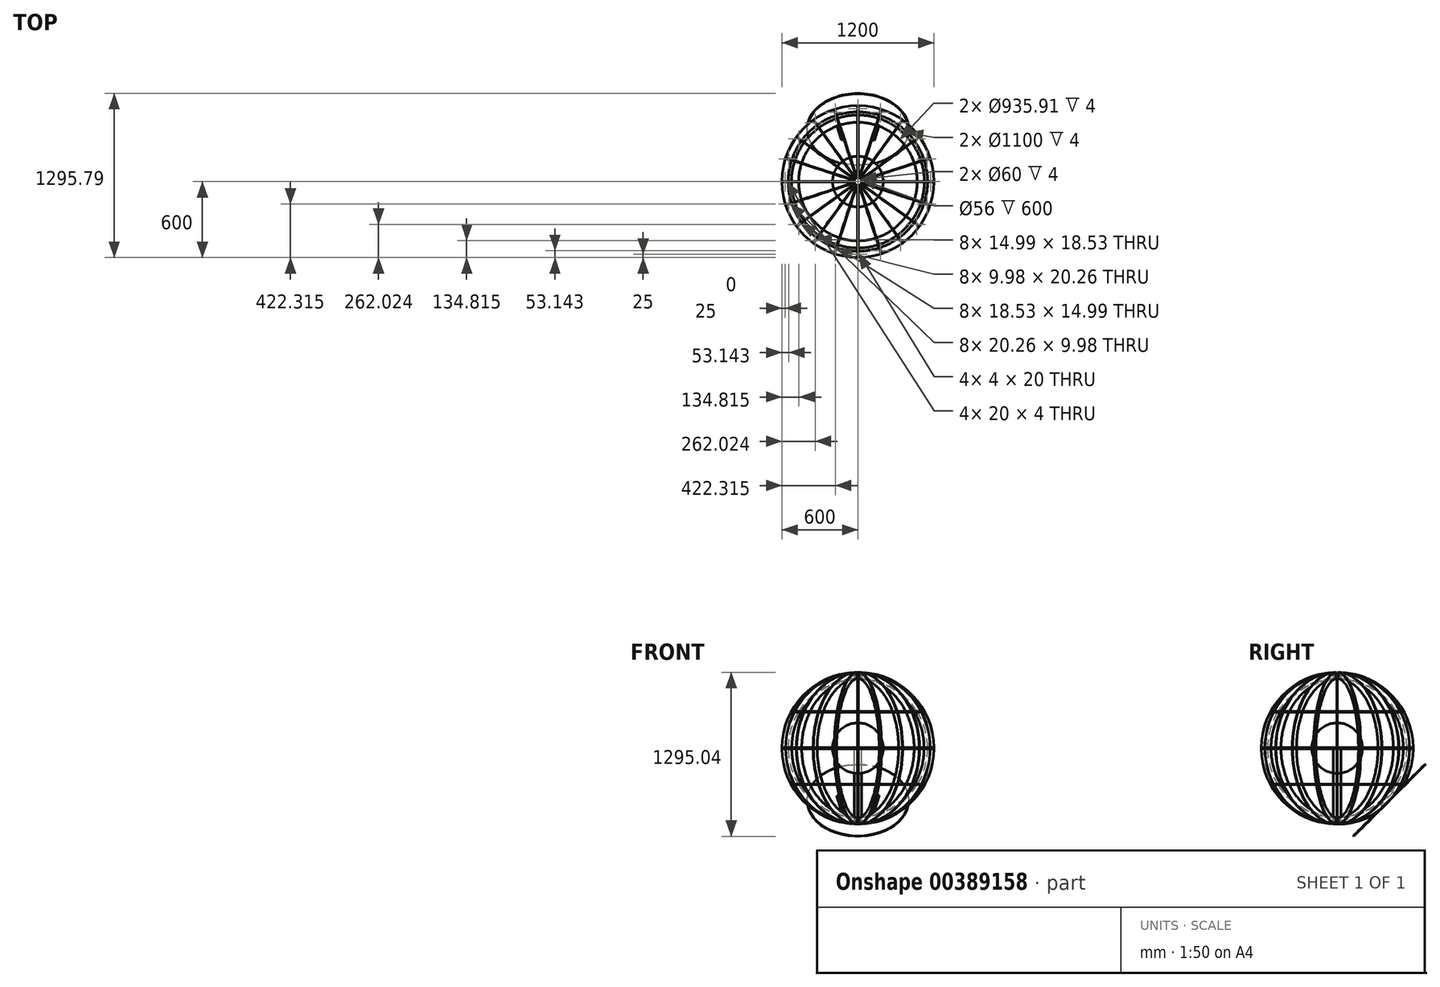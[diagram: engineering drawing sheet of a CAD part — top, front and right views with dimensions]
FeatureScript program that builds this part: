
annotation { "Feature Type Name" : "Feature", "Feature Type Description" : "" }
export const myFeature = defineFeature(function(context is Context, id is Id, definition is map)
    precondition{}
    {
        {
            var Q0;
            Q0=qCreatedBy(makeId("Front.planeOp"),FACE);
            var sketch = newSketch(context, id + "F0", { "sketchPlane" : qUnion([Q0])});
            skArc(sketch, "E0", {"start": v(-600, 0) * mm, "mid": v(-424.26, -424.26) * mm, "end": v(0, -600) * mm});
            skArc(sketch, "E1", {"start": v(-550, 0) * mm, "mid": v(-529.88, -147.4) * mm, "end": v(-471, -284) * mm});
            skLineSegment(sketch, "E2", {"start": v(0, 0) * mm, "end": v(0, -799.31) * mm});
            skLineSegment(sketch, "E3", {"start": v(0, 0) * mm, "end": v(-600, 0) * mm});
            skLineSegment(sketch, "E4", {"start": v(-599.99, -4) * mm, "end": v(-585, -4) * mm});
            skLineSegment(sketch, "E5", {"start": v(-585, -4) * mm, "end": v(-585, -2) * mm});
            skLineSegment(sketch, "E6", {"start": v(-585, -2) * mm, "end": v(-565, -2) * mm});
            skLineSegment(sketch, "E7", {"start": v(-565, -2) * mm, "end": v(-565, -4) * mm});
            skLineSegment(sketch, "E8", {"start": v(-565, -4) * mm, "end": v(-549.99, -4) * mm});
            skLineSegment(sketch, "E9", {"start": v(-30, -599.25) * mm, "end": v(-30, -549.18) * mm});
            skLineSegment(sketch, "E10", {"start": v(-30, -577.5) * mm, "end": v(-40, -577.5) * mm});
            skLineSegment(sketch, "E11", {"start": v(-40, -577.5) * mm, "end": v(-40, -572.5) * mm});
            skLineSegment(sketch, "E12", {"start": v(-40, -572.5) * mm, "end": v(-30, -572.5) * mm});
            skLineSegment(sketch, "E13", {"start": v(-471, -284) * mm, "end": v(-487.95, -284) * mm});
            skLineSegment(sketch, "E14", {"start": v(-487.95, -284) * mm, "end": v(-487.95, -289) * mm});
            skLineSegment(sketch, "E15", {"start": v(-487.95, -289) * mm, "end": v(-467.95, -289) * mm});
            skPoint(sketch, "E16", {"position": v(-467.95, -289) * mm});
            skLineSegment(sketch, "E17", {"start": v(-487.95, -289) * mm, "end": v(-567.03, -289) * mm, "construction": true});
            skPoint(sketch, "E18", {"position": v(-525.81, -289) * mm});
            skArc(sketch, "E19.trimOffspring", {"start": v(-467.95, -289) * mm, "mid": v(-267.9, -480.34) * mm, "end": v(0, -550) * mm});
            skSolve(sketch);
        }
        {
            var Q0;
            {var subQ12=sQuery(id+"F0.wireOp",EDGE,"E5");Q0=makeQuery(id+"F0.imprint","IMPRINT",FACE,{"disambiguationData":[TD([[makeQuery(id+"F0.imprint","IMPRINT",EDGE,{"derivedFrom":subQ12}),-1.0]])]});}
            extrude(context, id + "F1", {"entities" : qUnion([Q0]), "endBound" : BoundingType.SYMMETRIC, "depth" : 4 * mm});
        }
        {
            var Q0;
            Q0=qCreatedBy(makeId("Front.planeOp"),FACE);
            var sketch = newSketch(context, id + "F2", { "sketchPlane" : qUnion([Q0])});
            skLineSegment(sketch, "E20", {"start": v(0, -374.59) * mm, "end": v(0, 317) * mm});
            skSolve(sketch);
        }
        {
            var Q0;
            Q0=makeQuery(id+"F1.opExtrude","SWEPT_BODY",BODY,{"disambiguationData":[OSD([sQuery(id+"F0.wireOp",EDGE,"E0"),sQuery(id+"F0.wireOp",EDGE,"E1"),sQuery(id+"F0.wireOp",EDGE,"E4"),sQuery(id+"F0.wireOp",EDGE,"E5"),sQuery(id+"F0.wireOp",EDGE,"E6"),sQuery(id+"F0.wireOp",EDGE,"E7"),sQuery(id+"F0.wireOp",EDGE,"E8"),sQuery(id+"F0.wireOp",EDGE,"E9"),sQuery(id+"F0.wireOp",EDGE,"E10"),sQuery(id+"F0.wireOp",EDGE,"E11"),sQuery(id+"F0.wireOp",EDGE,"E12")])]});
            var Q1;
            Q1=sQuery(id+"F2.wireOp",EDGE,"E20");
            circularPattern(context, id + "F3", {"entities" : qUnion([Q0]), "axis" : qUnion([Q1]), "angle" : 360 * degree, "instanceCount" : 20, "equalSpace" : true});
        }
        {
            var Q0;
            Q0=qCreatedBy(makeId("Top.planeOp"),FACE);
            var sketch = newSketch(context, id + "F4", { "sketchPlane" : qUnion([Q0])});
            skLineSegment(sketch, "E21.0.0", {"start": v(-330.48, 458.27) * mm, "end": v(-342.24, 474.45) * mm});
            skLineSegment(sketch, "E21.0.1", {"start": v(-342.24, 474.45) * mm, "end": v(-345.47, 472.1) * mm});
            skLineSegment(sketch, "E21.0.2", {"start": v(-345.47, 472.1) * mm, "end": v(-333.72, 455.92) * mm});
            skLineSegment(sketch, "E21.0.3", {"start": v(-333.72, 455.92) * mm, "end": v(-330.48, 458.27) * mm});
            skLineSegment(sketch, "E22.0.0", {"start": v(-172.7, 537.96) * mm, "end": v(-178.87, 556.99) * mm});
            skLineSegment(sketch, "E22.0.1", {"start": v(-178.87, 556.99) * mm, "end": v(-182.68, 555.75) * mm});
            skLineSegment(sketch, "E22.0.2", {"start": v(-182.68, 555.75) * mm, "end": v(-176.5, 536.73) * mm});
            skLineSegment(sketch, "E22.0.3", {"start": v(-176.5, 536.73) * mm, "end": v(-172.7, 537.96) * mm});
            skLineSegment(sketch, "E23.0.0", {"start": v(2, 565) * mm, "end": v(2, 585) * mm});
            skLineSegment(sketch, "E23.0.1", {"start": v(2, 585) * mm, "end": v(-2, 585) * mm});
            skLineSegment(sketch, "E23.0.2", {"start": v(-2, 585) * mm, "end": v(-2, 565) * mm});
            skLineSegment(sketch, "E23.0.3", {"start": v(-2, 565) * mm, "end": v(2, 565) * mm});
            skLineSegment(sketch, "E24.0.0", {"start": v(176.5, 536.73) * mm, "end": v(182.68, 555.75) * mm});
            skLineSegment(sketch, "E24.0.1", {"start": v(182.68, 555.75) * mm, "end": v(178.87, 556.99) * mm});
            skLineSegment(sketch, "E24.0.2", {"start": v(178.87, 556.99) * mm, "end": v(172.7, 537.96) * mm});
            skLineSegment(sketch, "E24.0.3", {"start": v(172.7, 537.96) * mm, "end": v(176.5, 536.73) * mm});
            skLineSegment(sketch, "E25.0.0", {"start": v(333.72, 455.92) * mm, "end": v(345.47, 472.1) * mm});
            skLineSegment(sketch, "E25.0.1", {"start": v(345.47, 472.1) * mm, "end": v(342.24, 474.45) * mm});
            skLineSegment(sketch, "E25.0.2", {"start": v(342.24, 474.45) * mm, "end": v(330.48, 458.27) * mm});
            skLineSegment(sketch, "E25.0.3", {"start": v(330.48, 458.27) * mm, "end": v(333.72, 455.92) * mm});
            skLineSegment(sketch, "E26.0.0", {"start": v(458.27, 330.48) * mm, "end": v(474.45, 342.24) * mm});
            skLineSegment(sketch, "E26.0.1", {"start": v(474.45, 342.24) * mm, "end": v(472.1, 345.47) * mm});
            skLineSegment(sketch, "E26.0.2", {"start": v(472.1, 345.47) * mm, "end": v(455.92, 333.72) * mm});
            skLineSegment(sketch, "E26.0.3", {"start": v(455.92, 333.72) * mm, "end": v(458.27, 330.48) * mm});
            skLineSegment(sketch, "E27.0.0", {"start": v(537.96, 172.7) * mm, "end": v(556.99, 178.87) * mm});
            skLineSegment(sketch, "E27.0.1", {"start": v(556.99, 178.87) * mm, "end": v(555.75, 182.68) * mm});
            skLineSegment(sketch, "E27.0.2", {"start": v(555.75, 182.68) * mm, "end": v(536.73, 176.5) * mm});
            skLineSegment(sketch, "E27.0.3", {"start": v(536.73, 176.5) * mm, "end": v(537.96, 172.7) * mm});
            skLineSegment(sketch, "E28.0.0", {"start": v(565, -2) * mm, "end": v(585, -2) * mm});
            skLineSegment(sketch, "E28.0.1", {"start": v(585, -2) * mm, "end": v(585, 2) * mm});
            skLineSegment(sketch, "E28.0.2", {"start": v(585, 2) * mm, "end": v(565, 2) * mm});
            skLineSegment(sketch, "E28.0.3", {"start": v(565, 2) * mm, "end": v(565, -2) * mm});
            skLineSegment(sketch, "E29.0.0", {"start": v(536.73, -176.5) * mm, "end": v(555.75, -182.68) * mm});
            skLineSegment(sketch, "E29.0.1", {"start": v(555.75, -182.68) * mm, "end": v(556.99, -178.87) * mm});
            skLineSegment(sketch, "E29.0.2", {"start": v(556.99, -178.87) * mm, "end": v(537.96, -172.7) * mm});
            skLineSegment(sketch, "E29.0.3", {"start": v(537.96, -172.7) * mm, "end": v(536.73, -176.5) * mm});
            skLineSegment(sketch, "E30.0.0", {"start": v(455.92, -333.72) * mm, "end": v(472.1, -345.47) * mm});
            skLineSegment(sketch, "E30.0.1", {"start": v(472.1, -345.47) * mm, "end": v(474.45, -342.24) * mm});
            skLineSegment(sketch, "E30.0.2", {"start": v(474.45, -342.24) * mm, "end": v(458.27, -330.48) * mm});
            skLineSegment(sketch, "E30.0.3", {"start": v(458.27, -330.48) * mm, "end": v(455.92, -333.72) * mm});
            skLineSegment(sketch, "E31.0.0", {"start": v(330.48, -458.27) * mm, "end": v(342.24, -474.45) * mm});
            skLineSegment(sketch, "E31.0.1", {"start": v(342.24, -474.45) * mm, "end": v(345.47, -472.1) * mm});
            skLineSegment(sketch, "E31.0.2", {"start": v(345.47, -472.1) * mm, "end": v(333.72, -455.92) * mm});
            skLineSegment(sketch, "E31.0.3", {"start": v(333.72, -455.92) * mm, "end": v(330.48, -458.27) * mm});
            skLineSegment(sketch, "E32.0.0", {"start": v(172.7, -537.96) * mm, "end": v(178.87, -556.99) * mm});
            skLineSegment(sketch, "E32.0.1", {"start": v(178.87, -556.99) * mm, "end": v(182.68, -555.75) * mm});
            skLineSegment(sketch, "E32.0.2", {"start": v(182.68, -555.75) * mm, "end": v(176.5, -536.73) * mm});
            skLineSegment(sketch, "E32.0.3", {"start": v(176.5, -536.73) * mm, "end": v(172.7, -537.96) * mm});
            skLineSegment(sketch, "E33.0.0", {"start": v(-2, -565) * mm, "end": v(-2, -585) * mm});
            skLineSegment(sketch, "E33.0.1", {"start": v(-2, -585) * mm, "end": v(2, -585) * mm});
            skLineSegment(sketch, "E33.0.2", {"start": v(2, -585) * mm, "end": v(2, -565) * mm});
            skLineSegment(sketch, "E33.0.3", {"start": v(2, -565) * mm, "end": v(-2, -565) * mm});
            skLineSegment(sketch, "E34.0.0", {"start": v(-176.5, -536.73) * mm, "end": v(-182.68, -555.75) * mm});
            skLineSegment(sketch, "E34.0.1", {"start": v(-182.68, -555.75) * mm, "end": v(-178.87, -556.99) * mm});
            skLineSegment(sketch, "E34.0.2", {"start": v(-178.87, -556.99) * mm, "end": v(-172.7, -537.96) * mm});
            skLineSegment(sketch, "E34.0.3", {"start": v(-172.7, -537.96) * mm, "end": v(-176.5, -536.73) * mm});
            skLineSegment(sketch, "E35.0.0", {"start": v(-333.72, -455.92) * mm, "end": v(-345.47, -472.1) * mm});
            skLineSegment(sketch, "E35.0.1", {"start": v(-345.47, -472.1) * mm, "end": v(-342.24, -474.45) * mm});
            skLineSegment(sketch, "E35.0.2", {"start": v(-342.24, -474.45) * mm, "end": v(-330.48, -458.27) * mm});
            skLineSegment(sketch, "E35.0.3", {"start": v(-330.48, -458.27) * mm, "end": v(-333.72, -455.92) * mm});
            skLineSegment(sketch, "E36.0.0", {"start": v(-458.27, -330.48) * mm, "end": v(-474.45, -342.24) * mm});
            skLineSegment(sketch, "E36.0.1", {"start": v(-474.45, -342.24) * mm, "end": v(-472.1, -345.47) * mm});
            skLineSegment(sketch, "E36.0.2", {"start": v(-472.1, -345.47) * mm, "end": v(-455.92, -333.72) * mm});
            skLineSegment(sketch, "E36.0.3", {"start": v(-455.92, -333.72) * mm, "end": v(-458.27, -330.48) * mm});
            skLineSegment(sketch, "E37.0.0", {"start": v(-537.96, -172.7) * mm, "end": v(-556.99, -178.87) * mm});
            skLineSegment(sketch, "E37.0.1", {"start": v(-556.99, -178.87) * mm, "end": v(-555.75, -182.68) * mm});
            skLineSegment(sketch, "E37.0.2", {"start": v(-555.75, -182.68) * mm, "end": v(-536.73, -176.5) * mm});
            skLineSegment(sketch, "E37.0.3", {"start": v(-536.73, -176.5) * mm, "end": v(-537.96, -172.7) * mm});
            skLineSegment(sketch, "E38.0.0", {"start": v(-565, 2) * mm, "end": v(-585, 2) * mm});
            skLineSegment(sketch, "E38.0.1", {"start": v(-585, 2) * mm, "end": v(-585, -2) * mm});
            skLineSegment(sketch, "E38.0.2", {"start": v(-585, -2) * mm, "end": v(-565, -2) * mm});
            skLineSegment(sketch, "E38.0.3", {"start": v(-565, -2) * mm, "end": v(-565, 2) * mm});
            skLineSegment(sketch, "E39.0.0", {"start": v(-536.73, 176.5) * mm, "end": v(-555.75, 182.68) * mm});
            skLineSegment(sketch, "E39.0.1", {"start": v(-555.75, 182.68) * mm, "end": v(-556.99, 178.87) * mm});
            skLineSegment(sketch, "E39.0.2", {"start": v(-556.99, 178.87) * mm, "end": v(-537.96, 172.7) * mm});
            skLineSegment(sketch, "E39.0.3", {"start": v(-537.96, 172.7) * mm, "end": v(-536.73, 176.5) * mm});
            skLineSegment(sketch, "E40.0.0", {"start": v(-455.92, 333.72) * mm, "end": v(-472.1, 345.47) * mm});
            skLineSegment(sketch, "E40.0.1", {"start": v(-472.1, 345.47) * mm, "end": v(-474.45, 342.24) * mm});
            skLineSegment(sketch, "E40.0.2", {"start": v(-474.45, 342.24) * mm, "end": v(-458.27, 330.48) * mm});
            skLineSegment(sketch, "E40.0.3", {"start": v(-458.27, 330.48) * mm, "end": v(-455.92, 333.72) * mm});
            skCircle(sketch, "E41", {"center": v(0, 0) * mm, "radius": 600 * mm});
            skCircle(sketch, "E42", {"center": v(0, 0) * mm, "radius": 550 * mm});
            skSolve(sketch);
        }
        {
            var Q0;
            Q0=makeQuery(id+"F4.imprint","IMPRINT",FACE,{"disambiguationData":[TD([[makeQuery(id+"F4.imprint","IMPRINT",EDGE,{"derivedFrom":sQuery(id+"F4.wireOp",EDGE,"E21.0.0")}),-1.0]])]});
            extrude(context, id + "F5", {"entities" : qUnion([Q0]), "oppositeDirection" : true, "depth" : 4 * mm});
        }
        {
            var Q0;
            Q0=makeQuery(id+"F3.opPattern","COPY",FACE,{"derivedFrom":makeQuery(id+"F1.opExtrude","SWEPT_FACE",FACE,{"disambiguationData":[OSD([sQuery(id+"F0.wireOp",EDGE,"E12")])]}),"instanceName":"17"});
            var sketch = newSketch(context, id + "F6", { "sketchPlane" : qUnion([Q0])});
            skLineSegment(sketch, "E43.0.0", {"start": v(-31.19, -25.13) * mm, "end": v(-23.1, -19.25) * mm});
            skLineSegment(sketch, "E43.0.1", {"start": v(-23.1, -19.25) * mm, "end": v(-25.45, -16.02) * mm});
            skLineSegment(sketch, "E43.0.2", {"start": v(-25.45, -16.02) * mm, "end": v(-33.54, -21.9) * mm});
            skLineSegment(sketch, "E43.0.3", {"start": v(-33.54, -21.9) * mm, "end": v(-31.19, -25.13) * mm});
            skLineSegment(sketch, "E44.0.0", {"start": v(-37.42, -14.26) * mm, "end": v(-27.91, -11.17) * mm});
            skLineSegment(sketch, "E44.0.1", {"start": v(-27.91, -11.17) * mm, "end": v(-29.15, -7.37) * mm});
            skLineSegment(sketch, "E44.0.2", {"start": v(-29.15, -7.37) * mm, "end": v(-38.66, -10.46) * mm});
            skLineSegment(sketch, "E44.0.3", {"start": v(-38.66, -10.46) * mm, "end": v(-37.42, -14.26) * mm});
            skLineSegment(sketch, "E45.0.0", {"start": v(-10.46, -38.66) * mm, "end": v(-7.37, -29.15) * mm});
            skLineSegment(sketch, "E45.0.1", {"start": v(-7.37, -29.15) * mm, "end": v(-11.17, -27.91) * mm});
            skLineSegment(sketch, "E45.0.2", {"start": v(-11.17, -27.91) * mm, "end": v(-14.26, -37.42) * mm});
            skLineSegment(sketch, "E45.0.3", {"start": v(-14.26, -37.42) * mm, "end": v(-10.46, -38.66) * mm});
            skLineSegment(sketch, "E46.0.0", {"start": v(2, -40) * mm, "end": v(2, -30) * mm});
            skLineSegment(sketch, "E46.0.1", {"start": v(2, -30) * mm, "end": v(-2, -30) * mm});
            skLineSegment(sketch, "E46.0.2", {"start": v(-2, -30) * mm, "end": v(-2, -40) * mm});
            skLineSegment(sketch, "E46.0.3", {"start": v(-2, -40) * mm, "end": v(2, -40) * mm});
            skLineSegment(sketch, "E47.0.0", {"start": v(14.26, -37.42) * mm, "end": v(11.17, -27.91) * mm});
            skLineSegment(sketch, "E47.0.1", {"start": v(11.17, -27.91) * mm, "end": v(7.37, -29.15) * mm});
            skLineSegment(sketch, "E47.0.2", {"start": v(7.37, -29.15) * mm, "end": v(10.46, -38.66) * mm});
            skLineSegment(sketch, "E47.0.3", {"start": v(10.46, -38.66) * mm, "end": v(14.26, -37.42) * mm});
            skLineSegment(sketch, "E48.0", {"start": v(-25.13, -31.19) * mm, "end": v(-19.25, -23.1) * mm});
            skLineSegment(sketch, "E49.0", {"start": v(-25.13, -31.19) * mm, "end": v(-21.9, -33.54) * mm});
            skLineSegment(sketch, "E50.0", {"start": v(-21.9, -33.54) * mm, "end": v(-16.02, -25.45) * mm});
            skLineSegment(sketch, "E51.0", {"start": v(-19.25, -23.1) * mm, "end": v(-16.02, -25.45) * mm});
            skLineSegment(sketch, "E52.0.0", {"start": v(25.13, -31.19) * mm, "end": v(19.25, -23.1) * mm});
            skLineSegment(sketch, "E52.0.1", {"start": v(19.25, -23.1) * mm, "end": v(16.02, -25.45) * mm});
            skLineSegment(sketch, "E52.0.2", {"start": v(16.02, -25.45) * mm, "end": v(21.9, -33.54) * mm});
            skLineSegment(sketch, "E52.0.3", {"start": v(21.9, -33.54) * mm, "end": v(25.13, -31.19) * mm});
            skLineSegment(sketch, "E53.0.0", {"start": v(33.54, -21.9) * mm, "end": v(25.45, -16.02) * mm});
            skLineSegment(sketch, "E53.0.1", {"start": v(25.45, -16.02) * mm, "end": v(23.1, -19.25) * mm});
            skLineSegment(sketch, "E53.0.2", {"start": v(23.1, -19.25) * mm, "end": v(31.19, -25.13) * mm});
            skLineSegment(sketch, "E53.0.3", {"start": v(31.19, -25.13) * mm, "end": v(33.54, -21.9) * mm});
            skLineSegment(sketch, "E54.0.0", {"start": v(38.66, -10.46) * mm, "end": v(29.15, -7.37) * mm});
            skLineSegment(sketch, "E54.0.1", {"start": v(29.15, -7.37) * mm, "end": v(27.91, -11.17) * mm});
            skLineSegment(sketch, "E54.0.2", {"start": v(27.91, -11.17) * mm, "end": v(37.42, -14.26) * mm});
            skLineSegment(sketch, "E54.0.3", {"start": v(37.42, -14.26) * mm, "end": v(38.66, -10.46) * mm});
            skLineSegment(sketch, "E55.0.0", {"start": v(40, 2) * mm, "end": v(30, 2) * mm});
            skLineSegment(sketch, "E55.0.1", {"start": v(30, 2) * mm, "end": v(30, -2) * mm});
            skLineSegment(sketch, "E55.0.2", {"start": v(30, -2) * mm, "end": v(40, -2) * mm});
            skLineSegment(sketch, "E55.0.3", {"start": v(40, -2) * mm, "end": v(40, 2) * mm});
            skLineSegment(sketch, "E56.0.0", {"start": v(37.42, 14.26) * mm, "end": v(27.91, 11.17) * mm});
            skLineSegment(sketch, "E56.0.1", {"start": v(27.91, 11.17) * mm, "end": v(29.15, 7.37) * mm});
            skLineSegment(sketch, "E56.0.2", {"start": v(29.15, 7.37) * mm, "end": v(38.66, 10.46) * mm});
            skLineSegment(sketch, "E56.0.3", {"start": v(38.66, 10.46) * mm, "end": v(37.42, 14.26) * mm});
            skLineSegment(sketch, "E57.0.0", {"start": v(31.19, 25.13) * mm, "end": v(23.1, 19.25) * mm});
            skLineSegment(sketch, "E57.0.1", {"start": v(23.1, 19.25) * mm, "end": v(25.45, 16.02) * mm});
            skLineSegment(sketch, "E57.0.2", {"start": v(25.45, 16.02) * mm, "end": v(33.54, 21.9) * mm});
            skLineSegment(sketch, "E57.0.3", {"start": v(33.54, 21.9) * mm, "end": v(31.19, 25.13) * mm});
            skLineSegment(sketch, "E58.0.0", {"start": v(21.9, 33.54) * mm, "end": v(16.02, 25.45) * mm});
            skLineSegment(sketch, "E58.0.1", {"start": v(16.02, 25.45) * mm, "end": v(19.25, 23.1) * mm});
            skLineSegment(sketch, "E58.0.2", {"start": v(19.25, 23.1) * mm, "end": v(25.13, 31.19) * mm});
            skLineSegment(sketch, "E58.0.3", {"start": v(25.13, 31.19) * mm, "end": v(21.9, 33.54) * mm});
            skLineSegment(sketch, "E59.0.0", {"start": v(10.46, 38.66) * mm, "end": v(7.37, 29.15) * mm});
            skLineSegment(sketch, "E59.0.1", {"start": v(7.37, 29.15) * mm, "end": v(11.17, 27.91) * mm});
            skLineSegment(sketch, "E59.0.2", {"start": v(11.17, 27.91) * mm, "end": v(14.26, 37.42) * mm});
            skLineSegment(sketch, "E59.0.3", {"start": v(14.26, 37.42) * mm, "end": v(10.46, 38.66) * mm});
            skLineSegment(sketch, "E60.0.0", {"start": v(-2, 40) * mm, "end": v(-2, 30) * mm});
            skLineSegment(sketch, "E60.0.1", {"start": v(-2, 30) * mm, "end": v(2, 30) * mm});
            skLineSegment(sketch, "E60.0.2", {"start": v(2, 30) * mm, "end": v(2, 40) * mm});
            skLineSegment(sketch, "E60.0.3", {"start": v(2, 40) * mm, "end": v(-2, 40) * mm});
            skLineSegment(sketch, "E61.0.0", {"start": v(-14.26, 37.42) * mm, "end": v(-11.17, 27.91) * mm});
            skLineSegment(sketch, "E61.0.1", {"start": v(-11.17, 27.91) * mm, "end": v(-7.37, 29.15) * mm});
            skLineSegment(sketch, "E61.0.2", {"start": v(-7.37, 29.15) * mm, "end": v(-10.46, 38.66) * mm});
            skLineSegment(sketch, "E61.0.3", {"start": v(-10.46, 38.66) * mm, "end": v(-14.26, 37.42) * mm});
            skLineSegment(sketch, "E62.0.0", {"start": v(-25.13, 31.19) * mm, "end": v(-19.25, 23.1) * mm});
            skLineSegment(sketch, "E62.0.1", {"start": v(-19.25, 23.1) * mm, "end": v(-16.02, 25.45) * mm});
            skLineSegment(sketch, "E62.0.2", {"start": v(-16.02, 25.45) * mm, "end": v(-21.9, 33.54) * mm});
            skLineSegment(sketch, "E62.0.3", {"start": v(-21.9, 33.54) * mm, "end": v(-25.13, 31.19) * mm});
            skLineSegment(sketch, "E63.0.0", {"start": v(-33.54, 21.9) * mm, "end": v(-25.45, 16.02) * mm});
            skLineSegment(sketch, "E63.0.1", {"start": v(-25.45, 16.02) * mm, "end": v(-23.1, 19.25) * mm});
            skLineSegment(sketch, "E63.0.2", {"start": v(-23.1, 19.25) * mm, "end": v(-31.19, 25.13) * mm});
            skLineSegment(sketch, "E63.0.3", {"start": v(-31.19, 25.13) * mm, "end": v(-33.54, 21.9) * mm});
            skLineSegment(sketch, "E64.0.0", {"start": v(-38.66, 10.46) * mm, "end": v(-29.15, 7.37) * mm});
            skLineSegment(sketch, "E64.0.1", {"start": v(-29.15, 7.37) * mm, "end": v(-27.91, 11.17) * mm});
            skLineSegment(sketch, "E64.0.2", {"start": v(-27.91, 11.17) * mm, "end": v(-37.42, 14.26) * mm});
            skLineSegment(sketch, "E64.0.3", {"start": v(-37.42, 14.26) * mm, "end": v(-38.66, 10.46) * mm});
            skLineSegment(sketch, "E65.0.0", {"start": v(-40, -2) * mm, "end": v(-30, -2) * mm});
            skLineSegment(sketch, "E65.0.1", {"start": v(-30, -2) * mm, "end": v(-30, 2) * mm});
            skLineSegment(sketch, "E65.0.2", {"start": v(-30, 2) * mm, "end": v(-40, 2) * mm});
            skLineSegment(sketch, "E65.0.3", {"start": v(-40, 2) * mm, "end": v(-40, -2) * mm});
            skCircle(sketch, "E66", {"center": v(0, 0) * mm, "radius": 30 * mm});
            skArc(sketch, "E67", {"start": v(-15.8, 42.14) * mm, "mid": v(-20.43, 40.1) * mm, "end": v(-24.8, 37.55) * mm});
            skLineSegment(sketch, "E68", {"start": v(-2, 40) * mm, "end": v(-2, 44.96) * mm});
            skLineSegment(sketch, "E69", {"start": v(2, 40) * mm, "end": v(2, 44.96) * mm});
            skLineSegment(sketch, "E70", {"start": v(10.46, 38.66) * mm, "end": v(11.99, 43.37) * mm});
            skLineSegment(sketch, "E71", {"start": v(14.26, 37.42) * mm, "end": v(15.8, 42.14) * mm});
            skLineSegment(sketch, "E72", {"start": v(21.9, 33.54) * mm, "end": v(24.8, 37.55) * mm});
            skLineSegment(sketch, "E73", {"start": v(25.13, 31.19) * mm, "end": v(28.04, 35.2) * mm});
            skLineSegment(sketch, "E74", {"start": v(31.19, 25.13) * mm, "end": v(35.2, 28.04) * mm});
            skLineSegment(sketch, "E75", {"start": v(33.54, 21.9) * mm, "end": v(37.55, 24.8) * mm});
            skLineSegment(sketch, "E76", {"start": v(37.42, 14.26) * mm, "end": v(42.14, 15.8) * mm});
            skLineSegment(sketch, "E77", {"start": v(38.66, 10.46) * mm, "end": v(43.37, 11.99) * mm});
            skLineSegment(sketch, "E78", {"start": v(-14.26, 37.42) * mm, "end": v(-15.8, 42.14) * mm});
            skLineSegment(sketch, "E79", {"start": v(-10.46, 38.66) * mm, "end": v(-11.99, 43.37) * mm});
            skArc(sketch, "E80.trimOffspring", {"start": v(-2, 44.96) * mm, "mid": v(-7.04, 44.45) * mm, "end": v(-11.99, 43.37) * mm});
            skArc(sketch, "E81.trimOffspring", {"start": v(11.99, 43.37) * mm, "mid": v(7.04, 44.45) * mm, "end": v(2, 44.96) * mm});
            skArc(sketch, "E82.trimOffspring", {"start": v(24.8, 37.55) * mm, "mid": v(20.43, 40.1) * mm, "end": v(15.8, 42.14) * mm});
            skArc(sketch, "E83.trimOffspring", {"start": v(35.2, 28.04) * mm, "mid": v(31.82, 31.82) * mm, "end": v(28.04, 35.2) * mm});
            skArc(sketch, "E84.trimOffspring", {"start": v(42.14, 15.8) * mm, "mid": v(40.1, 20.43) * mm, "end": v(37.55, 24.8) * mm});
            skLineSegment(sketch, "E85", {"start": v(40, 2) * mm, "end": v(44.96, 2) * mm});
            skLineSegment(sketch, "E86", {"start": v(40, -2) * mm, "end": v(44.96, -2) * mm});
            skLineSegment(sketch, "E87", {"start": v(38.66, -10.46) * mm, "end": v(43.37, -11.99) * mm});
            skLineSegment(sketch, "E88", {"start": v(37.42, -14.26) * mm, "end": v(42.14, -15.8) * mm});
            skLineSegment(sketch, "E89", {"start": v(33.54, -21.9) * mm, "end": v(37.55, -24.8) * mm});
            skLineSegment(sketch, "E90", {"start": v(31.19, -25.13) * mm, "end": v(35.2, -28.04) * mm});
            skLineSegment(sketch, "E91", {"start": v(25.13, -31.19) * mm, "end": v(28.04, -35.2) * mm});
            skLineSegment(sketch, "E92", {"start": v(21.9, -33.54) * mm, "end": v(24.8, -37.55) * mm});
            skLineSegment(sketch, "E93", {"start": v(14.26, -37.42) * mm, "end": v(15.8, -42.14) * mm});
            skLineSegment(sketch, "E94", {"start": v(10.46, -38.66) * mm, "end": v(11.99, -43.37) * mm});
            skLineSegment(sketch, "E95", {"start": v(2, -40) * mm, "end": v(2, -44.96) * mm});
            skLineSegment(sketch, "E96", {"start": v(-2, -40) * mm, "end": v(-2, -44.96) * mm});
            skArc(sketch, "E97.trimOffspring", {"start": v(15.8, -42.14) * mm, "mid": v(20.43, -40.1) * mm, "end": v(24.8, -37.55) * mm});
            skArc(sketch, "E98.trimOffspring", {"start": v(28.04, -35.2) * mm, "mid": v(31.82, -31.82) * mm, "end": v(35.2, -28.04) * mm});
            skArc(sketch, "E99.trimOffspring", {"start": v(37.55, -24.8) * mm, "mid": v(40.1, -20.43) * mm, "end": v(42.14, -15.8) * mm});
            skArc(sketch, "E100.trimOffspring", {"start": v(43.37, -11.99) * mm, "mid": v(44.45, -7.04) * mm, "end": v(44.96, -2) * mm});
            skArc(sketch, "E101.trimOffspring", {"start": v(44.96, 2) * mm, "mid": v(44.45, 7.04) * mm, "end": v(43.37, 11.99) * mm});
            skArc(sketch, "E102.trimOffspring", {"start": v(2, -44.96) * mm, "mid": v(7.04, -44.45) * mm, "end": v(11.99, -43.37) * mm});
            skLineSegment(sketch, "E103", {"start": v(-10.46, -38.66) * mm, "end": v(-11.99, -43.37) * mm});
            skLineSegment(sketch, "E104", {"start": v(-14.26, -37.42) * mm, "end": v(-15.8, -42.14) * mm});
            skLineSegment(sketch, "E105", {"start": v(-21.9, -33.54) * mm, "end": v(-24.8, -37.55) * mm});
            skLineSegment(sketch, "E106", {"start": v(-25.13, -31.19) * mm, "end": v(-28.04, -35.2) * mm});
            skLineSegment(sketch, "E107", {"start": v(-31.19, -25.13) * mm, "end": v(-35.2, -28.04) * mm});
            skLineSegment(sketch, "E108", {"start": v(-33.54, -21.9) * mm, "end": v(-37.55, -24.8) * mm});
            skLineSegment(sketch, "E109", {"start": v(-37.42, -14.26) * mm, "end": v(-42.14, -15.8) * mm});
            skLineSegment(sketch, "E110", {"start": v(-38.66, -10.46) * mm, "end": v(-43.37, -11.99) * mm});
            skArc(sketch, "E111.trimOffspring", {"start": v(-42.14, -15.8) * mm, "mid": v(-40.1, -20.43) * mm, "end": v(-37.55, -24.8) * mm});
            skArc(sketch, "E112.trimOffspring", {"start": v(-35.2, -28.04) * mm, "mid": v(-31.82, -31.82) * mm, "end": v(-28.04, -35.2) * mm});
            skArc(sketch, "E113.trimOffspring", {"start": v(-24.8, -37.55) * mm, "mid": v(-20.43, -40.1) * mm, "end": v(-15.8, -42.14) * mm});
            skArc(sketch, "E114.trimOffspring", {"start": v(-11.99, -43.37) * mm, "mid": v(-7.04, -44.45) * mm, "end": v(-2, -44.96) * mm});
            skLineSegment(sketch, "E115", {"start": v(-40, -2) * mm, "end": v(-44.96, -2) * mm});
            skLineSegment(sketch, "E116", {"start": v(-40, 2) * mm, "end": v(-44.96, 2) * mm});
            skLineSegment(sketch, "E117", {"start": v(-38.66, 10.46) * mm, "end": v(-43.37, 11.99) * mm});
            skLineSegment(sketch, "E118", {"start": v(-37.42, 14.26) * mm, "end": v(-42.14, 15.8) * mm});
            skLineSegment(sketch, "E119", {"start": v(-33.54, 21.9) * mm, "end": v(-37.55, 24.8) * mm});
            skLineSegment(sketch, "E120", {"start": v(-31.19, 25.13) * mm, "end": v(-35.2, 28.04) * mm});
            skLineSegment(sketch, "E121", {"start": v(-25.13, 31.19) * mm, "end": v(-28.04, 35.2) * mm});
            skLineSegment(sketch, "E122", {"start": v(-21.9, 33.54) * mm, "end": v(-24.8, 37.55) * mm});
            skArc(sketch, "E123.trimOffspring", {"start": v(-44.96, -2) * mm, "mid": v(-44.45, -7.04) * mm, "end": v(-43.37, -11.99) * mm});
            skArc(sketch, "E124.trimOffspring", {"start": v(-43.37, 11.99) * mm, "mid": v(-44.45, 7.04) * mm, "end": v(-44.96, 2) * mm});
            skArc(sketch, "E125.trimOffspring", {"start": v(-37.55, 24.8) * mm, "mid": v(-40.1, 20.43) * mm, "end": v(-42.14, 15.8) * mm});
            skArc(sketch, "E126.trimOffspring", {"start": v(-28.04, 35.2) * mm, "mid": v(-31.82, 31.82) * mm, "end": v(-35.2, 28.04) * mm});
            skSolve(sketch);
        }
        {
            var Q0;
            Q0 = qSketchRegion(id + "F6", true);
            extrude(context, id + "F7", {"entities" : qUnion([Q0]), "depth" : 4 * mm});
        }
        {
            var Q0;
            Q0=makeQuery(id+"F3.opPattern","COPY",FACE,{"derivedFrom":makeQuery(id+"F1.opExtrude","SWEPT_FACE",FACE,{"disambiguationData":[OSD([sQuery(id+"F0.wireOp",EDGE,"E15")])]}),"instanceName":"7"});
            var sketch = newSketch(context, id + "F8", { "sketchPlane" : qUnion([Q0])});
            skLineSegment(sketch, "E127.0", {"start": v(288.43, -393.59) * mm, "end": v(285.2, -395.94) * mm});
            skLineSegment(sketch, "E128.0", {"start": v(285.2, -395.94) * mm, "end": v(273.44, -379.76) * mm});
            skLineSegment(sketch, "E129.0", {"start": v(288.43, -393.59) * mm, "end": v(276.67, -377.4) * mm});
            skLineSegment(sketch, "E130.0", {"start": v(276.67, -377.4) * mm, "end": v(273.44, -379.76) * mm});
            skLineSegment(sketch, "E131.1.0", {"start": v(379.76, -273.44) * mm, "end": v(377.4, -276.67) * mm});
            skLineSegment(sketch, "E131.1.1", {"start": v(393.59, -288.43) * mm, "end": v(377.4, -276.67) * mm});
            skLineSegment(sketch, "E131.1.2", {"start": v(395.94, -285.2) * mm, "end": v(379.76, -273.44) * mm});
            skLineSegment(sketch, "E131.1.3", {"start": v(395.94, -285.2) * mm, "end": v(393.59, -288.43) * mm});
            skLineSegment(sketch, "E131.2.0", {"start": v(445.67, -142.7) * mm, "end": v(444.43, -146.5) * mm});
            skLineSegment(sketch, "E131.2.1", {"start": v(463.45, -152.69) * mm, "end": v(444.43, -146.5) * mm});
            skLineSegment(sketch, "E131.2.2", {"start": v(464.69, -148.88) * mm, "end": v(445.67, -142.7) * mm});
            skLineSegment(sketch, "E131.2.3", {"start": v(464.69, -148.88) * mm, "end": v(463.45, -152.69) * mm});
            skLineSegment(sketch, "E131.3.0", {"start": v(467.95, 2) * mm, "end": v(467.95, -2) * mm});
            skLineSegment(sketch, "E131.3.1", {"start": v(487.95, -2) * mm, "end": v(467.95, -2) * mm});
            skLineSegment(sketch, "E131.3.2", {"start": v(487.95, 2) * mm, "end": v(467.95, 2) * mm});
            skLineSegment(sketch, "E131.3.3", {"start": v(487.95, 2) * mm, "end": v(487.95, -2) * mm});
            skLineSegment(sketch, "E131.4.0", {"start": v(444.43, 146.5) * mm, "end": v(445.67, 142.7) * mm});
            skLineSegment(sketch, "E131.4.1", {"start": v(464.69, 148.88) * mm, "end": v(445.67, 142.7) * mm});
            skLineSegment(sketch, "E131.4.2", {"start": v(463.45, 152.69) * mm, "end": v(444.43, 146.5) * mm});
            skLineSegment(sketch, "E131.4.3", {"start": v(463.45, 152.69) * mm, "end": v(464.69, 148.88) * mm});
            skLineSegment(sketch, "E131.5.0", {"start": v(377.4, 276.67) * mm, "end": v(379.76, 273.44) * mm});
            skLineSegment(sketch, "E131.5.1", {"start": v(395.94, 285.2) * mm, "end": v(379.76, 273.44) * mm});
            skLineSegment(sketch, "E131.5.2", {"start": v(393.59, 288.43) * mm, "end": v(377.4, 276.67) * mm});
            skLineSegment(sketch, "E131.5.3", {"start": v(393.59, 288.43) * mm, "end": v(395.94, 285.2) * mm});
            skLineSegment(sketch, "E131.6.0", {"start": v(273.44, 379.76) * mm, "end": v(276.67, 377.4) * mm});
            skLineSegment(sketch, "E131.6.1", {"start": v(288.43, 393.59) * mm, "end": v(276.67, 377.4) * mm});
            skLineSegment(sketch, "E131.6.2", {"start": v(285.2, 395.94) * mm, "end": v(273.44, 379.76) * mm});
            skLineSegment(sketch, "E131.6.3", {"start": v(285.2, 395.94) * mm, "end": v(288.43, 393.59) * mm});
            skLineSegment(sketch, "E131.7.0", {"start": v(142.7, 445.67) * mm, "end": v(146.5, 444.43) * mm});
            skLineSegment(sketch, "E131.7.1", {"start": v(152.69, 463.45) * mm, "end": v(146.5, 444.43) * mm});
            skLineSegment(sketch, "E131.7.2", {"start": v(148.88, 464.69) * mm, "end": v(142.7, 445.67) * mm});
            skLineSegment(sketch, "E131.7.3", {"start": v(148.88, 464.69) * mm, "end": v(152.69, 463.45) * mm});
            skLineSegment(sketch, "E131.8.0", {"start": v(-2, 467.95) * mm, "end": v(2, 467.95) * mm});
            skLineSegment(sketch, "E131.8.1", {"start": v(2, 487.95) * mm, "end": v(2, 467.95) * mm});
            skLineSegment(sketch, "E131.8.2", {"start": v(-2, 487.95) * mm, "end": v(-2, 467.95) * mm});
            skLineSegment(sketch, "E131.8.3", {"start": v(-2, 487.95) * mm, "end": v(2, 487.95) * mm});
            skLineSegment(sketch, "E131.9.0", {"start": v(-146.5, 444.43) * mm, "end": v(-142.7, 445.67) * mm});
            skLineSegment(sketch, "E131.9.1", {"start": v(-148.88, 464.69) * mm, "end": v(-142.7, 445.67) * mm});
            skLineSegment(sketch, "E131.9.2", {"start": v(-152.69, 463.45) * mm, "end": v(-146.5, 444.43) * mm});
            skLineSegment(sketch, "E131.9.3", {"start": v(-152.69, 463.45) * mm, "end": v(-148.88, 464.69) * mm});
            skLineSegment(sketch, "E131.10.0", {"start": v(-276.67, 377.4) * mm, "end": v(-273.44, 379.76) * mm});
            skLineSegment(sketch, "E131.10.1", {"start": v(-285.2, 395.94) * mm, "end": v(-273.44, 379.76) * mm});
            skLineSegment(sketch, "E131.10.2", {"start": v(-288.43, 393.59) * mm, "end": v(-276.67, 377.4) * mm});
            skLineSegment(sketch, "E131.10.3", {"start": v(-288.43, 393.59) * mm, "end": v(-285.2, 395.94) * mm});
            skLineSegment(sketch, "E131.11.0", {"start": v(-379.76, 273.44) * mm, "end": v(-377.4, 276.67) * mm});
            skLineSegment(sketch, "E131.11.1", {"start": v(-393.59, 288.43) * mm, "end": v(-377.4, 276.67) * mm});
            skLineSegment(sketch, "E131.11.2", {"start": v(-395.94, 285.2) * mm, "end": v(-379.76, 273.44) * mm});
            skLineSegment(sketch, "E131.11.3", {"start": v(-395.94, 285.2) * mm, "end": v(-393.59, 288.43) * mm});
            skLineSegment(sketch, "E131.12.0", {"start": v(-445.67, 142.7) * mm, "end": v(-444.43, 146.5) * mm});
            skLineSegment(sketch, "E131.12.1", {"start": v(-463.45, 152.69) * mm, "end": v(-444.43, 146.5) * mm});
            skLineSegment(sketch, "E131.12.2", {"start": v(-464.69, 148.88) * mm, "end": v(-445.67, 142.7) * mm});
            skLineSegment(sketch, "E131.12.3", {"start": v(-464.69, 148.88) * mm, "end": v(-463.45, 152.69) * mm});
            skLineSegment(sketch, "E131.13.0", {"start": v(-467.95, -2) * mm, "end": v(-467.95, 2) * mm});
            skLineSegment(sketch, "E131.13.1", {"start": v(-487.95, 2) * mm, "end": v(-467.95, 2) * mm});
            skLineSegment(sketch, "E131.13.2", {"start": v(-487.95, -2) * mm, "end": v(-467.95, -2) * mm});
            skLineSegment(sketch, "E131.13.3", {"start": v(-487.95, -2) * mm, "end": v(-487.95, 2) * mm});
            skLineSegment(sketch, "E131.14.0", {"start": v(-444.43, -146.5) * mm, "end": v(-445.67, -142.7) * mm});
            skLineSegment(sketch, "E131.14.1", {"start": v(-464.69, -148.88) * mm, "end": v(-445.67, -142.7) * mm});
            skLineSegment(sketch, "E131.14.2", {"start": v(-463.45, -152.69) * mm, "end": v(-444.43, -146.5) * mm});
            skLineSegment(sketch, "E131.14.3", {"start": v(-463.45, -152.69) * mm, "end": v(-464.69, -148.88) * mm});
            skLineSegment(sketch, "E131.15.0", {"start": v(-377.4, -276.67) * mm, "end": v(-379.76, -273.44) * mm});
            skLineSegment(sketch, "E131.15.1", {"start": v(-395.94, -285.2) * mm, "end": v(-379.76, -273.44) * mm});
            skLineSegment(sketch, "E131.15.2", {"start": v(-393.59, -288.43) * mm, "end": v(-377.4, -276.67) * mm});
            skLineSegment(sketch, "E131.15.3", {"start": v(-393.59, -288.43) * mm, "end": v(-395.94, -285.2) * mm});
            skLineSegment(sketch, "E131.16.0", {"start": v(-273.44, -379.76) * mm, "end": v(-276.67, -377.4) * mm});
            skLineSegment(sketch, "E131.16.1", {"start": v(-288.43, -393.59) * mm, "end": v(-276.67, -377.4) * mm});
            skLineSegment(sketch, "E131.16.2", {"start": v(-285.2, -395.94) * mm, "end": v(-273.44, -379.76) * mm});
            skLineSegment(sketch, "E131.16.3", {"start": v(-285.2, -395.94) * mm, "end": v(-288.43, -393.59) * mm});
            skLineSegment(sketch, "E131.17.0", {"start": v(-142.7, -445.67) * mm, "end": v(-146.5, -444.43) * mm});
            skLineSegment(sketch, "E131.17.1", {"start": v(-152.69, -463.45) * mm, "end": v(-146.5, -444.43) * mm});
            skLineSegment(sketch, "E131.17.2", {"start": v(-148.88, -464.69) * mm, "end": v(-142.7, -445.67) * mm});
            skLineSegment(sketch, "E131.17.3", {"start": v(-148.88, -464.69) * mm, "end": v(-152.69, -463.45) * mm});
            skLineSegment(sketch, "E131.18.0", {"start": v(2, -467.95) * mm, "end": v(-2, -467.95) * mm});
            skLineSegment(sketch, "E131.18.1", {"start": v(-2, -487.95) * mm, "end": v(-2, -467.95) * mm});
            skLineSegment(sketch, "E131.18.2", {"start": v(2, -487.95) * mm, "end": v(2, -467.95) * mm});
            skLineSegment(sketch, "E131.18.3", {"start": v(2, -487.95) * mm, "end": v(-2, -487.95) * mm});
            skLineSegment(sketch, "E131.19.0", {"start": v(146.5, -444.43) * mm, "end": v(142.7, -445.67) * mm});
            skLineSegment(sketch, "E131.19.1", {"start": v(148.88, -464.69) * mm, "end": v(142.7, -445.67) * mm});
            skLineSegment(sketch, "E131.19.2", {"start": v(152.69, -463.45) * mm, "end": v(146.5, -444.43) * mm});
            skLineSegment(sketch, "E131.19.3", {"start": v(152.69, -463.45) * mm, "end": v(148.88, -464.69) * mm});
            skPoint(sketch, "E131.center", {"position": v(0, 0) * mm});
            skCircle(sketch, "E132", {"center": v(0, 0) * mm, "radius": 467.96 * mm});
            skArc(sketch, "E133", {"start": v(2, -525) * mm, "mid": v(82.13, -518.54) * mm, "end": v(160.33, -499.92) * mm});
            skLineSegment(sketch, "E134", {"start": v(-2, -487.95) * mm, "end": v(-2, -525) * mm});
            skLineSegment(sketch, "E135", {"start": v(2, -487.95) * mm, "end": v(2, -525) * mm});
            skLineSegment(sketch, "E136.1.0", {"start": v(148.88, -464.69) * mm, "end": v(160.33, -499.92) * mm});
            skLineSegment(sketch, "E136.1.1", {"start": v(152.69, -463.45) * mm, "end": v(164.13, -498.68) * mm});
            skLineSegment(sketch, "E136.2.0", {"start": v(285.2, -395.94) * mm, "end": v(306.97, -425.9) * mm});
            skLineSegment(sketch, "E136.2.1", {"start": v(288.43, -393.59) * mm, "end": v(310.2, -423.56) * mm});
            skLineSegment(sketch, "E136.3.0", {"start": v(393.59, -288.43) * mm, "end": v(423.56, -310.2) * mm});
            skLineSegment(sketch, "E136.3.1", {"start": v(395.94, -285.2) * mm, "end": v(425.9, -306.97) * mm});
            skLineSegment(sketch, "E136.4.0", {"start": v(463.45, -152.69) * mm, "end": v(498.68, -164.13) * mm});
            skLineSegment(sketch, "E136.4.1", {"start": v(464.69, -148.88) * mm, "end": v(499.92, -160.33) * mm});
            skLineSegment(sketch, "E136.5.0", {"start": v(487.95, -2) * mm, "end": v(525, -2) * mm});
            skLineSegment(sketch, "E136.5.1", {"start": v(487.95, 2) * mm, "end": v(525, 2) * mm});
            skLineSegment(sketch, "E136.6.0", {"start": v(464.69, 148.88) * mm, "end": v(499.92, 160.33) * mm});
            skLineSegment(sketch, "E136.6.1", {"start": v(463.45, 152.69) * mm, "end": v(498.68, 164.13) * mm});
            skLineSegment(sketch, "E136.7.0", {"start": v(395.94, 285.2) * mm, "end": v(425.9, 306.97) * mm});
            skLineSegment(sketch, "E136.7.1", {"start": v(393.59, 288.43) * mm, "end": v(423.56, 310.2) * mm});
            skLineSegment(sketch, "E136.8.0", {"start": v(288.43, 393.59) * mm, "end": v(310.2, 423.56) * mm});
            skLineSegment(sketch, "E136.8.1", {"start": v(285.2, 395.94) * mm, "end": v(306.97, 425.9) * mm});
            skLineSegment(sketch, "E136.9.0", {"start": v(152.69, 463.45) * mm, "end": v(164.13, 498.68) * mm});
            skLineSegment(sketch, "E136.9.1", {"start": v(148.88, 464.69) * mm, "end": v(160.33, 499.92) * mm});
            skLineSegment(sketch, "E136.10.0", {"start": v(2, 487.95) * mm, "end": v(2, 525) * mm});
            skLineSegment(sketch, "E136.10.1", {"start": v(-2, 487.95) * mm, "end": v(-2, 525) * mm});
            skLineSegment(sketch, "E136.11.0", {"start": v(-148.88, 464.69) * mm, "end": v(-160.33, 499.92) * mm});
            skLineSegment(sketch, "E136.11.1", {"start": v(-152.69, 463.45) * mm, "end": v(-164.13, 498.68) * mm});
            skLineSegment(sketch, "E136.12.0", {"start": v(-285.2, 395.94) * mm, "end": v(-306.97, 425.9) * mm});
            skLineSegment(sketch, "E136.12.1", {"start": v(-288.43, 393.59) * mm, "end": v(-310.2, 423.56) * mm});
            skLineSegment(sketch, "E136.13.0", {"start": v(-393.59, 288.43) * mm, "end": v(-423.56, 310.2) * mm});
            skLineSegment(sketch, "E136.13.1", {"start": v(-395.94, 285.2) * mm, "end": v(-425.9, 306.97) * mm});
            skLineSegment(sketch, "E136.14.0", {"start": v(-463.45, 152.69) * mm, "end": v(-498.68, 164.13) * mm});
            skLineSegment(sketch, "E136.14.1", {"start": v(-464.69, 148.88) * mm, "end": v(-499.92, 160.33) * mm});
            skLineSegment(sketch, "E136.15.0", {"start": v(-487.95, 2) * mm, "end": v(-525, 2) * mm});
            skLineSegment(sketch, "E136.15.1", {"start": v(-487.95, -2) * mm, "end": v(-525, -2) * mm});
            skLineSegment(sketch, "E136.16.0", {"start": v(-464.69, -148.88) * mm, "end": v(-499.92, -160.33) * mm});
            skLineSegment(sketch, "E136.16.1", {"start": v(-463.45, -152.69) * mm, "end": v(-498.68, -164.13) * mm});
            skLineSegment(sketch, "E136.17.0", {"start": v(-395.94, -285.2) * mm, "end": v(-425.9, -306.97) * mm});
            skLineSegment(sketch, "E136.17.1", {"start": v(-393.59, -288.43) * mm, "end": v(-423.56, -310.2) * mm});
            skLineSegment(sketch, "E136.18.0", {"start": v(-288.43, -393.59) * mm, "end": v(-310.2, -423.56) * mm});
            skLineSegment(sketch, "E136.18.1", {"start": v(-285.2, -395.94) * mm, "end": v(-306.97, -425.9) * mm});
            skLineSegment(sketch, "E136.19.0", {"start": v(-152.69, -463.45) * mm, "end": v(-164.13, -498.68) * mm});
            skLineSegment(sketch, "E136.19.1", {"start": v(-148.88, -464.69) * mm, "end": v(-160.33, -499.92) * mm});
            skArc(sketch, "E137.trimOffspring", {"start": v(164.13, -498.68) * mm, "mid": v(238.35, -467.78) * mm, "end": v(306.97, -425.9) * mm});
            skArc(sketch, "E138.trimOffspring", {"start": v(310.2, -423.56) * mm, "mid": v(371.23, -371.23) * mm, "end": v(423.56, -310.2) * mm});
            skArc(sketch, "E139.trimOffspring", {"start": v(425.9, -306.97) * mm, "mid": v(467.78, -238.35) * mm, "end": v(498.68, -164.13) * mm});
            skArc(sketch, "E140.trimOffspring", {"start": v(499.92, -160.33) * mm, "mid": v(518.54, -82.13) * mm, "end": v(525, -2) * mm});
            skArc(sketch, "E141.trimOffspring", {"start": v(525, 2) * mm, "mid": v(518.54, 82.13) * mm, "end": v(499.92, 160.33) * mm});
            skArc(sketch, "E142.trimOffspring", {"start": v(498.68, 164.13) * mm, "mid": v(467.78, 238.35) * mm, "end": v(425.9, 306.97) * mm});
            skArc(sketch, "E143.trimOffspring", {"start": v(423.56, 310.2) * mm, "mid": v(371.23, 371.23) * mm, "end": v(310.2, 423.56) * mm});
            skArc(sketch, "E144.trimOffspring", {"start": v(306.97, 425.9) * mm, "mid": v(238.35, 467.78) * mm, "end": v(164.13, 498.68) * mm});
            skArc(sketch, "E145.trimOffspring", {"start": v(160.33, 499.92) * mm, "mid": v(82.13, 518.54) * mm, "end": v(2, 525) * mm});
            skArc(sketch, "E146.trimOffspring", {"start": v(-2, 525) * mm, "mid": v(-82.13, 518.54) * mm, "end": v(-160.33, 499.92) * mm});
            skArc(sketch, "E147.trimOffspring", {"start": v(-164.13, 498.68) * mm, "mid": v(-238.35, 467.78) * mm, "end": v(-306.97, 425.9) * mm});
            skArc(sketch, "E148.trimOffspring", {"start": v(-310.2, 423.56) * mm, "mid": v(-371.23, 371.23) * mm, "end": v(-423.56, 310.2) * mm});
            skArc(sketch, "E149.trimOffspring", {"start": v(-425.9, 306.97) * mm, "mid": v(-467.78, 238.35) * mm, "end": v(-498.68, 164.13) * mm});
            skArc(sketch, "E150.trimOffspring", {"start": v(-499.92, 160.33) * mm, "mid": v(-518.54, 82.13) * mm, "end": v(-525, 2) * mm});
            skArc(sketch, "E151.trimOffspring", {"start": v(-525, -2) * mm, "mid": v(-518.54, -82.13) * mm, "end": v(-499.92, -160.33) * mm});
            skArc(sketch, "E152.trimOffspring", {"start": v(-498.68, -164.13) * mm, "mid": v(-467.78, -238.35) * mm, "end": v(-425.9, -306.97) * mm});
            skArc(sketch, "E153.trimOffspring", {"start": v(-423.56, -310.2) * mm, "mid": v(-371.23, -371.23) * mm, "end": v(-310.2, -423.56) * mm});
            skArc(sketch, "E154.trimOffspring", {"start": v(-306.97, -425.9) * mm, "mid": v(-238.35, -467.78) * mm, "end": v(-164.13, -498.68) * mm});
            skArc(sketch, "E155.trimOffspring", {"start": v(-160.33, -499.92) * mm, "mid": v(-82.13, -518.54) * mm, "end": v(-2, -525) * mm});
            skSolve(sketch);
        }
        {
            var Q0;
            Q0 = qSketchRegion(id + "F8", true);
            extrude(context, id + "F9", {"entities" : qUnion([Q0]), "depth" : 4 * mm});
        }
        {
            var Q0;
            Q0=makeQuery(id+"F3.opPattern","COPY",BODY,{"derivedFrom":makeQuery(id+"F1.opExtrude","SWEPT_BODY",BODY,{"disambiguationData":[OSD([sQuery(id+"F0.wireOp",EDGE,"E0"),sQuery(id+"F0.wireOp",EDGE,"E1"),sQuery(id+"F0.wireOp",EDGE,"E4"),sQuery(id+"F0.wireOp",EDGE,"E5"),sQuery(id+"F0.wireOp",EDGE,"E6"),sQuery(id+"F0.wireOp",EDGE,"E7"),sQuery(id+"F0.wireOp",EDGE,"E8"),sQuery(id+"F0.wireOp",EDGE,"E9"),sQuery(id+"F0.wireOp",EDGE,"E10"),sQuery(id+"F0.wireOp",EDGE,"E11"),sQuery(id+"F0.wireOp",EDGE,"E12"),sQuery(id+"F0.wireOp",EDGE,"E13"),sQuery(id+"F0.wireOp",EDGE,"E14"),sQuery(id+"F0.wireOp",EDGE,"E15"),sQuery(id+"F0.wireOp",EDGE,"E19.trimOffspring")])]}),"instanceName":"17"});
            var Q1;
            Q1=makeQuery(id+"F1.opExtrude","SWEPT_BODY",BODY,{"disambiguationData":[OSD([sQuery(id+"F0.wireOp",EDGE,"E0"),sQuery(id+"F0.wireOp",EDGE,"E1"),sQuery(id+"F0.wireOp",EDGE,"E4"),sQuery(id+"F0.wireOp",EDGE,"E5"),sQuery(id+"F0.wireOp",EDGE,"E6"),sQuery(id+"F0.wireOp",EDGE,"E7"),sQuery(id+"F0.wireOp",EDGE,"E8"),sQuery(id+"F0.wireOp",EDGE,"E9"),sQuery(id+"F0.wireOp",EDGE,"E10"),sQuery(id+"F0.wireOp",EDGE,"E11"),sQuery(id+"F0.wireOp",EDGE,"E12"),sQuery(id+"F0.wireOp",EDGE,"E13"),sQuery(id+"F0.wireOp",EDGE,"E14"),sQuery(id+"F0.wireOp",EDGE,"E15"),sQuery(id+"F0.wireOp",EDGE,"E19.trimOffspring")])]});
            var Q2;
            Q2=makeQuery(id+"F3.opPattern","COPY",BODY,{"derivedFrom":makeQuery(id+"F1.opExtrude","SWEPT_BODY",BODY,{"disambiguationData":[OSD([sQuery(id+"F0.wireOp",EDGE,"E0"),sQuery(id+"F0.wireOp",EDGE,"E1"),sQuery(id+"F0.wireOp",EDGE,"E4"),sQuery(id+"F0.wireOp",EDGE,"E5"),sQuery(id+"F0.wireOp",EDGE,"E6"),sQuery(id+"F0.wireOp",EDGE,"E7"),sQuery(id+"F0.wireOp",EDGE,"E8"),sQuery(id+"F0.wireOp",EDGE,"E9"),sQuery(id+"F0.wireOp",EDGE,"E10"),sQuery(id+"F0.wireOp",EDGE,"E11"),sQuery(id+"F0.wireOp",EDGE,"E12"),sQuery(id+"F0.wireOp",EDGE,"E13"),sQuery(id+"F0.wireOp",EDGE,"E14"),sQuery(id+"F0.wireOp",EDGE,"E15"),sQuery(id+"F0.wireOp",EDGE,"E19.trimOffspring")])]}),"instanceName":"4"});
            var Q3;
            Q3=makeQuery(id+"F3.opPattern","COPY",BODY,{"derivedFrom":makeQuery(id+"F1.opExtrude","SWEPT_BODY",BODY,{"disambiguationData":[OSD([sQuery(id+"F0.wireOp",EDGE,"E0"),sQuery(id+"F0.wireOp",EDGE,"E1"),sQuery(id+"F0.wireOp",EDGE,"E4"),sQuery(id+"F0.wireOp",EDGE,"E5"),sQuery(id+"F0.wireOp",EDGE,"E6"),sQuery(id+"F0.wireOp",EDGE,"E7"),sQuery(id+"F0.wireOp",EDGE,"E8"),sQuery(id+"F0.wireOp",EDGE,"E9"),sQuery(id+"F0.wireOp",EDGE,"E10"),sQuery(id+"F0.wireOp",EDGE,"E11"),sQuery(id+"F0.wireOp",EDGE,"E12"),sQuery(id+"F0.wireOp",EDGE,"E13"),sQuery(id+"F0.wireOp",EDGE,"E14"),sQuery(id+"F0.wireOp",EDGE,"E15"),sQuery(id+"F0.wireOp",EDGE,"E19.trimOffspring")])]}),"instanceName":"2"});
            var Q4;
            Q4=makeQuery(id+"F3.opPattern","COPY",BODY,{"derivedFrom":makeQuery(id+"F1.opExtrude","SWEPT_BODY",BODY,{"disambiguationData":[OSD([sQuery(id+"F0.wireOp",EDGE,"E0"),sQuery(id+"F0.wireOp",EDGE,"E1"),sQuery(id+"F0.wireOp",EDGE,"E4"),sQuery(id+"F0.wireOp",EDGE,"E5"),sQuery(id+"F0.wireOp",EDGE,"E6"),sQuery(id+"F0.wireOp",EDGE,"E7"),sQuery(id+"F0.wireOp",EDGE,"E8"),sQuery(id+"F0.wireOp",EDGE,"E9"),sQuery(id+"F0.wireOp",EDGE,"E10"),sQuery(id+"F0.wireOp",EDGE,"E11"),sQuery(id+"F0.wireOp",EDGE,"E12"),sQuery(id+"F0.wireOp",EDGE,"E13"),sQuery(id+"F0.wireOp",EDGE,"E14"),sQuery(id+"F0.wireOp",EDGE,"E15"),sQuery(id+"F0.wireOp",EDGE,"E19.trimOffspring")])]}),"instanceName":"16"});
            var Q5;
            Q5=makeQuery(id+"F3.opPattern","COPY",BODY,{"derivedFrom":makeQuery(id+"F1.opExtrude","SWEPT_BODY",BODY,{"disambiguationData":[OSD([sQuery(id+"F0.wireOp",EDGE,"E0"),sQuery(id+"F0.wireOp",EDGE,"E1"),sQuery(id+"F0.wireOp",EDGE,"E4"),sQuery(id+"F0.wireOp",EDGE,"E5"),sQuery(id+"F0.wireOp",EDGE,"E6"),sQuery(id+"F0.wireOp",EDGE,"E7"),sQuery(id+"F0.wireOp",EDGE,"E8"),sQuery(id+"F0.wireOp",EDGE,"E9"),sQuery(id+"F0.wireOp",EDGE,"E10"),sQuery(id+"F0.wireOp",EDGE,"E11"),sQuery(id+"F0.wireOp",EDGE,"E12"),sQuery(id+"F0.wireOp",EDGE,"E13"),sQuery(id+"F0.wireOp",EDGE,"E14"),sQuery(id+"F0.wireOp",EDGE,"E15"),sQuery(id+"F0.wireOp",EDGE,"E19.trimOffspring")])]}),"instanceName":"19"});
            var Q6;
            Q6=makeQuery(id+"F3.opPattern","COPY",BODY,{"derivedFrom":makeQuery(id+"F1.opExtrude","SWEPT_BODY",BODY,{"disambiguationData":[OSD([sQuery(id+"F0.wireOp",EDGE,"E0"),sQuery(id+"F0.wireOp",EDGE,"E1"),sQuery(id+"F0.wireOp",EDGE,"E4"),sQuery(id+"F0.wireOp",EDGE,"E5"),sQuery(id+"F0.wireOp",EDGE,"E6"),sQuery(id+"F0.wireOp",EDGE,"E7"),sQuery(id+"F0.wireOp",EDGE,"E8"),sQuery(id+"F0.wireOp",EDGE,"E9"),sQuery(id+"F0.wireOp",EDGE,"E10"),sQuery(id+"F0.wireOp",EDGE,"E11"),sQuery(id+"F0.wireOp",EDGE,"E12"),sQuery(id+"F0.wireOp",EDGE,"E13"),sQuery(id+"F0.wireOp",EDGE,"E14"),sQuery(id+"F0.wireOp",EDGE,"E15"),sQuery(id+"F0.wireOp",EDGE,"E19.trimOffspring")])]}),"instanceName":"7"});
            var Q7;
            Q7=makeQuery(id+"F7.opExtrude","SWEPT_BODY",BODY,{"disambiguationData":[OSD([sQuery(id+"F6.wireOp",EDGE,"E43.0.3"),sQuery(id+"F6.wireOp",EDGE,"E44.0.3"),sQuery(id+"F6.wireOp",EDGE,"E45.0.3"),sQuery(id+"F6.wireOp",EDGE,"E46.0.3"),sQuery(id+"F6.wireOp",EDGE,"E47.0.3"),sQuery(id+"F6.wireOp",EDGE,"E49.0"),sQuery(id+"F6.wireOp",EDGE,"E52.0.3"),sQuery(id+"F6.wireOp",EDGE,"E53.0.3"),sQuery(id+"F6.wireOp",EDGE,"E54.0.3"),sQuery(id+"F6.wireOp",EDGE,"E55.0.3"),sQuery(id+"F6.wireOp",EDGE,"E56.0.3"),sQuery(id+"F6.wireOp",EDGE,"E57.0.3"),sQuery(id+"F6.wireOp",EDGE,"E58.0.3"),sQuery(id+"F6.wireOp",EDGE,"E59.0.3"),sQuery(id+"F6.wireOp",EDGE,"E60.0.3"),sQuery(id+"F6.wireOp",EDGE,"E61.0.3"),sQuery(id+"F6.wireOp",EDGE,"E62.0.3"),sQuery(id+"F6.wireOp",EDGE,"E63.0.3"),sQuery(id+"F6.wireOp",EDGE,"E64.0.3"),sQuery(id+"F6.wireOp",EDGE,"E65.0.3"),sQuery(id+"F6.wireOp",EDGE,"E66"),sQuery(id+"F6.wireOp",EDGE,"E67"),sQuery(id+"F6.wireOp",EDGE,"E68"),sQuery(id+"F6.wireOp",EDGE,"E69"),sQuery(id+"F6.wireOp",EDGE,"E70"),sQuery(id+"F6.wireOp",EDGE,"E71"),sQuery(id+"F6.wireOp",EDGE,"E72"),sQuery(id+"F6.wireOp",EDGE,"E73"),sQuery(id+"F6.wireOp",EDGE,"E74"),sQuery(id+"F6.wireOp",EDGE,"E75"),sQuery(id+"F6.wireOp",EDGE,"E76"),sQuery(id+"F6.wireOp",EDGE,"E77"),sQuery(id+"F6.wireOp",EDGE,"E78"),sQuery(id+"F6.wireOp",EDGE,"E79"),sQuery(id+"F6.wireOp",EDGE,"E80.trimOffspring"),sQuery(id+"F6.wireOp",EDGE,"E81.trimOffspring"),sQuery(id+"F6.wireOp",EDGE,"E82.trimOffspring"),sQuery(id+"F6.wireOp",EDGE,"E83.trimOffspring"),sQuery(id+"F6.wireOp",EDGE,"E84.trimOffspring"),sQuery(id+"F6.wireOp",EDGE,"E85"),sQuery(id+"F6.wireOp",EDGE,"E86"),sQuery(id+"F6.wireOp",EDGE,"E87"),sQuery(id+"F6.wireOp",EDGE,"E88"),sQuery(id+"F6.wireOp",EDGE,"E89"),sQuery(id+"F6.wireOp",EDGE,"E90"),sQuery(id+"F6.wireOp",EDGE,"E91"),sQuery(id+"F6.wireOp",EDGE,"E92"),sQuery(id+"F6.wireOp",EDGE,"E93"),sQuery(id+"F6.wireOp",EDGE,"E94"),sQuery(id+"F6.wireOp",EDGE,"E95"),sQuery(id+"F6.wireOp",EDGE,"E96"),sQuery(id+"F6.wireOp",EDGE,"E97.trimOffspring"),sQuery(id+"F6.wireOp",EDGE,"E98.trimOffspring"),sQuery(id+"F6.wireOp",EDGE,"E99.trimOffspring"),sQuery(id+"F6.wireOp",EDGE,"E100.trimOffspring"),sQuery(id+"F6.wireOp",EDGE,"E101.trimOffspring"),sQuery(id+"F6.wireOp",EDGE,"E102.trimOffspring"),sQuery(id+"F6.wireOp",EDGE,"E103"),sQuery(id+"F6.wireOp",EDGE,"E104"),sQuery(id+"F6.wireOp",EDGE,"E105"),sQuery(id+"F6.wireOp",EDGE,"E106"),sQuery(id+"F6.wireOp",EDGE,"E107"),sQuery(id+"F6.wireOp",EDGE,"E108"),sQuery(id+"F6.wireOp",EDGE,"E109"),sQuery(id+"F6.wireOp",EDGE,"E110"),sQuery(id+"F6.wireOp",EDGE,"E111.trimOffspring"),sQuery(id+"F6.wireOp",EDGE,"E112.trimOffspring"),sQuery(id+"F6.wireOp",EDGE,"E113.trimOffspring"),sQuery(id+"F6.wireOp",EDGE,"E114.trimOffspring"),sQuery(id+"F6.wireOp",EDGE,"E115"),sQuery(id+"F6.wireOp",EDGE,"E116"),sQuery(id+"F6.wireOp",EDGE,"E117"),sQuery(id+"F6.wireOp",EDGE,"E118"),sQuery(id+"F6.wireOp",EDGE,"E119"),sQuery(id+"F6.wireOp",EDGE,"E120"),sQuery(id+"F6.wireOp",EDGE,"E121"),sQuery(id+"F6.wireOp",EDGE,"E122"),sQuery(id+"F6.wireOp",EDGE,"E123.trimOffspring"),sQuery(id+"F6.wireOp",EDGE,"E124.trimOffspring"),sQuery(id+"F6.wireOp",EDGE,"E125.trimOffspring"),sQuery(id+"F6.wireOp",EDGE,"E126.trimOffspring")])]});
            var Q8;
            Q8=makeQuery(id+"F5.opExtrude","SWEPT_BODY",BODY,{"disambiguationData":[OSD([sQuery(id+"F4.wireOp",EDGE,"E21.0.0"),sQuery(id+"F4.wireOp",EDGE,"E21.0.1"),sQuery(id+"F4.wireOp",EDGE,"E21.0.2"),sQuery(id+"F4.wireOp",EDGE,"E21.0.3"),sQuery(id+"F4.wireOp",EDGE,"E22.0.0"),sQuery(id+"F4.wireOp",EDGE,"E22.0.1"),sQuery(id+"F4.wireOp",EDGE,"E22.0.2"),sQuery(id+"F4.wireOp",EDGE,"E22.0.3"),sQuery(id+"F4.wireOp",EDGE,"E23.0.0"),sQuery(id+"F4.wireOp",EDGE,"E23.0.1"),sQuery(id+"F4.wireOp",EDGE,"E23.0.2"),sQuery(id+"F4.wireOp",EDGE,"E23.0.3"),sQuery(id+"F4.wireOp",EDGE,"E24.0.0"),sQuery(id+"F4.wireOp",EDGE,"E24.0.1"),sQuery(id+"F4.wireOp",EDGE,"E24.0.2"),sQuery(id+"F4.wireOp",EDGE,"E24.0.3"),sQuery(id+"F4.wireOp",EDGE,"E25.0.0"),sQuery(id+"F4.wireOp",EDGE,"E25.0.1"),sQuery(id+"F4.wireOp",EDGE,"E25.0.2"),sQuery(id+"F4.wireOp",EDGE,"E25.0.3"),sQuery(id+"F4.wireOp",EDGE,"E26.0.0"),sQuery(id+"F4.wireOp",EDGE,"E26.0.1"),sQuery(id+"F4.wireOp",EDGE,"E26.0.2"),sQuery(id+"F4.wireOp",EDGE,"E26.0.3"),sQuery(id+"F4.wireOp",EDGE,"E27.0.0"),sQuery(id+"F4.wireOp",EDGE,"E27.0.1"),sQuery(id+"F4.wireOp",EDGE,"E27.0.2"),sQuery(id+"F4.wireOp",EDGE,"E27.0.3"),sQuery(id+"F4.wireOp",EDGE,"E28.0.0"),sQuery(id+"F4.wireOp",EDGE,"E28.0.1"),sQuery(id+"F4.wireOp",EDGE,"E28.0.2"),sQuery(id+"F4.wireOp",EDGE,"E28.0.3"),sQuery(id+"F4.wireOp",EDGE,"E29.0.0"),sQuery(id+"F4.wireOp",EDGE,"E29.0.1"),sQuery(id+"F4.wireOp",EDGE,"E29.0.2"),sQuery(id+"F4.wireOp",EDGE,"E29.0.3"),sQuery(id+"F4.wireOp",EDGE,"E30.0.0"),sQuery(id+"F4.wireOp",EDGE,"E30.0.1"),sQuery(id+"F4.wireOp",EDGE,"E30.0.2"),sQuery(id+"F4.wireOp",EDGE,"E30.0.3"),sQuery(id+"F4.wireOp",EDGE,"E31.0.0"),sQuery(id+"F4.wireOp",EDGE,"E31.0.1"),sQuery(id+"F4.wireOp",EDGE,"E31.0.2"),sQuery(id+"F4.wireOp",EDGE,"E31.0.3"),sQuery(id+"F4.wireOp",EDGE,"E32.0.0"),sQuery(id+"F4.wireOp",EDGE,"E32.0.1"),sQuery(id+"F4.wireOp",EDGE,"E32.0.2"),sQuery(id+"F4.wireOp",EDGE,"E32.0.3"),sQuery(id+"F4.wireOp",EDGE,"E33.0.0"),sQuery(id+"F4.wireOp",EDGE,"E33.0.1"),sQuery(id+"F4.wireOp",EDGE,"E33.0.2"),sQuery(id+"F4.wireOp",EDGE,"E33.0.3"),sQuery(id+"F4.wireOp",EDGE,"E34.0.0"),sQuery(id+"F4.wireOp",EDGE,"E34.0.1"),sQuery(id+"F4.wireOp",EDGE,"E34.0.2"),sQuery(id+"F4.wireOp",EDGE,"E34.0.3"),sQuery(id+"F4.wireOp",EDGE,"E35.0.0"),sQuery(id+"F4.wireOp",EDGE,"E35.0.1"),sQuery(id+"F4.wireOp",EDGE,"E35.0.2"),sQuery(id+"F4.wireOp",EDGE,"E35.0.3"),sQuery(id+"F4.wireOp",EDGE,"E36.0.0"),sQuery(id+"F4.wireOp",EDGE,"E36.0.1"),sQuery(id+"F4.wireOp",EDGE,"E36.0.2"),sQuery(id+"F4.wireOp",EDGE,"E36.0.3"),sQuery(id+"F4.wireOp",EDGE,"E37.0.0"),sQuery(id+"F4.wireOp",EDGE,"E37.0.1"),sQuery(id+"F4.wireOp",EDGE,"E37.0.2"),sQuery(id+"F4.wireOp",EDGE,"E37.0.3"),sQuery(id+"F4.wireOp",EDGE,"E38.0.0"),sQuery(id+"F4.wireOp",EDGE,"E38.0.1"),sQuery(id+"F4.wireOp",EDGE,"E38.0.2"),sQuery(id+"F4.wireOp",EDGE,"E38.0.3"),sQuery(id+"F4.wireOp",EDGE,"E39.0.0"),sQuery(id+"F4.wireOp",EDGE,"E39.0.1"),sQuery(id+"F4.wireOp",EDGE,"E39.0.2"),sQuery(id+"F4.wireOp",EDGE,"E39.0.3"),sQuery(id+"F4.wireOp",EDGE,"E40.0.0"),sQuery(id+"F4.wireOp",EDGE,"E40.0.1"),sQuery(id+"F4.wireOp",EDGE,"E40.0.2"),sQuery(id+"F4.wireOp",EDGE,"E40.0.3"),sQuery(id+"F4.wireOp",EDGE,"E41"),sQuery(id+"F4.wireOp",EDGE,"E42")])]});
            var Q9;
            Q9=makeQuery(id+"F3.opPattern","COPY",BODY,{"derivedFrom":makeQuery(id+"F1.opExtrude","SWEPT_BODY",BODY,{"disambiguationData":[OSD([sQuery(id+"F0.wireOp",EDGE,"E0"),sQuery(id+"F0.wireOp",EDGE,"E1"),sQuery(id+"F0.wireOp",EDGE,"E4"),sQuery(id+"F0.wireOp",EDGE,"E5"),sQuery(id+"F0.wireOp",EDGE,"E6"),sQuery(id+"F0.wireOp",EDGE,"E7"),sQuery(id+"F0.wireOp",EDGE,"E8"),sQuery(id+"F0.wireOp",EDGE,"E9"),sQuery(id+"F0.wireOp",EDGE,"E10"),sQuery(id+"F0.wireOp",EDGE,"E11"),sQuery(id+"F0.wireOp",EDGE,"E12"),sQuery(id+"F0.wireOp",EDGE,"E13"),sQuery(id+"F0.wireOp",EDGE,"E14"),sQuery(id+"F0.wireOp",EDGE,"E15"),sQuery(id+"F0.wireOp",EDGE,"E19.trimOffspring")])]}),"instanceName":"3"});
            var Q10;
            Q10=makeQuery(id+"F3.opPattern","COPY",BODY,{"derivedFrom":makeQuery(id+"F1.opExtrude","SWEPT_BODY",BODY,{"disambiguationData":[OSD([sQuery(id+"F0.wireOp",EDGE,"E0"),sQuery(id+"F0.wireOp",EDGE,"E1"),sQuery(id+"F0.wireOp",EDGE,"E4"),sQuery(id+"F0.wireOp",EDGE,"E5"),sQuery(id+"F0.wireOp",EDGE,"E6"),sQuery(id+"F0.wireOp",EDGE,"E7"),sQuery(id+"F0.wireOp",EDGE,"E8"),sQuery(id+"F0.wireOp",EDGE,"E9"),sQuery(id+"F0.wireOp",EDGE,"E10"),sQuery(id+"F0.wireOp",EDGE,"E11"),sQuery(id+"F0.wireOp",EDGE,"E12"),sQuery(id+"F0.wireOp",EDGE,"E13"),sQuery(id+"F0.wireOp",EDGE,"E14"),sQuery(id+"F0.wireOp",EDGE,"E15"),sQuery(id+"F0.wireOp",EDGE,"E19.trimOffspring")])]}),"instanceName":"1"});
            var Q11;
            Q11=makeQuery(id+"F3.opPattern","COPY",BODY,{"derivedFrom":makeQuery(id+"F1.opExtrude","SWEPT_BODY",BODY,{"disambiguationData":[OSD([sQuery(id+"F0.wireOp",EDGE,"E0"),sQuery(id+"F0.wireOp",EDGE,"E1"),sQuery(id+"F0.wireOp",EDGE,"E4"),sQuery(id+"F0.wireOp",EDGE,"E5"),sQuery(id+"F0.wireOp",EDGE,"E6"),sQuery(id+"F0.wireOp",EDGE,"E7"),sQuery(id+"F0.wireOp",EDGE,"E8"),sQuery(id+"F0.wireOp",EDGE,"E9"),sQuery(id+"F0.wireOp",EDGE,"E10"),sQuery(id+"F0.wireOp",EDGE,"E11"),sQuery(id+"F0.wireOp",EDGE,"E12"),sQuery(id+"F0.wireOp",EDGE,"E13"),sQuery(id+"F0.wireOp",EDGE,"E14"),sQuery(id+"F0.wireOp",EDGE,"E15"),sQuery(id+"F0.wireOp",EDGE,"E19.trimOffspring")])]}),"instanceName":"6"});
            var Q12;
            Q12=makeQuery(id+"F3.opPattern","COPY",BODY,{"derivedFrom":makeQuery(id+"F1.opExtrude","SWEPT_BODY",BODY,{"disambiguationData":[OSD([sQuery(id+"F0.wireOp",EDGE,"E0"),sQuery(id+"F0.wireOp",EDGE,"E1"),sQuery(id+"F0.wireOp",EDGE,"E4"),sQuery(id+"F0.wireOp",EDGE,"E5"),sQuery(id+"F0.wireOp",EDGE,"E6"),sQuery(id+"F0.wireOp",EDGE,"E7"),sQuery(id+"F0.wireOp",EDGE,"E8"),sQuery(id+"F0.wireOp",EDGE,"E9"),sQuery(id+"F0.wireOp",EDGE,"E10"),sQuery(id+"F0.wireOp",EDGE,"E11"),sQuery(id+"F0.wireOp",EDGE,"E12"),sQuery(id+"F0.wireOp",EDGE,"E13"),sQuery(id+"F0.wireOp",EDGE,"E14"),sQuery(id+"F0.wireOp",EDGE,"E15"),sQuery(id+"F0.wireOp",EDGE,"E19.trimOffspring")])]}),"instanceName":"8"});
            var Q13;
            Q13=makeQuery(id+"F3.opPattern","COPY",BODY,{"derivedFrom":makeQuery(id+"F1.opExtrude","SWEPT_BODY",BODY,{"disambiguationData":[OSD([sQuery(id+"F0.wireOp",EDGE,"E0"),sQuery(id+"F0.wireOp",EDGE,"E1"),sQuery(id+"F0.wireOp",EDGE,"E4"),sQuery(id+"F0.wireOp",EDGE,"E5"),sQuery(id+"F0.wireOp",EDGE,"E6"),sQuery(id+"F0.wireOp",EDGE,"E7"),sQuery(id+"F0.wireOp",EDGE,"E8"),sQuery(id+"F0.wireOp",EDGE,"E9"),sQuery(id+"F0.wireOp",EDGE,"E10"),sQuery(id+"F0.wireOp",EDGE,"E11"),sQuery(id+"F0.wireOp",EDGE,"E12"),sQuery(id+"F0.wireOp",EDGE,"E13"),sQuery(id+"F0.wireOp",EDGE,"E14"),sQuery(id+"F0.wireOp",EDGE,"E15"),sQuery(id+"F0.wireOp",EDGE,"E19.trimOffspring")])]}),"instanceName":"14"});
            var Q14;
            Q14=makeQuery(id+"F3.opPattern","COPY",BODY,{"derivedFrom":makeQuery(id+"F1.opExtrude","SWEPT_BODY",BODY,{"disambiguationData":[OSD([sQuery(id+"F0.wireOp",EDGE,"E0"),sQuery(id+"F0.wireOp",EDGE,"E1"),sQuery(id+"F0.wireOp",EDGE,"E4"),sQuery(id+"F0.wireOp",EDGE,"E5"),sQuery(id+"F0.wireOp",EDGE,"E6"),sQuery(id+"F0.wireOp",EDGE,"E7"),sQuery(id+"F0.wireOp",EDGE,"E8"),sQuery(id+"F0.wireOp",EDGE,"E9"),sQuery(id+"F0.wireOp",EDGE,"E10"),sQuery(id+"F0.wireOp",EDGE,"E11"),sQuery(id+"F0.wireOp",EDGE,"E12"),sQuery(id+"F0.wireOp",EDGE,"E13"),sQuery(id+"F0.wireOp",EDGE,"E14"),sQuery(id+"F0.wireOp",EDGE,"E15"),sQuery(id+"F0.wireOp",EDGE,"E19.trimOffspring")])]}),"instanceName":"5"});
            var Q15;
            Q15=makeQuery(id+"F3.opPattern","COPY",BODY,{"derivedFrom":makeQuery(id+"F1.opExtrude","SWEPT_BODY",BODY,{"disambiguationData":[OSD([sQuery(id+"F0.wireOp",EDGE,"E0"),sQuery(id+"F0.wireOp",EDGE,"E1"),sQuery(id+"F0.wireOp",EDGE,"E4"),sQuery(id+"F0.wireOp",EDGE,"E5"),sQuery(id+"F0.wireOp",EDGE,"E6"),sQuery(id+"F0.wireOp",EDGE,"E7"),sQuery(id+"F0.wireOp",EDGE,"E8"),sQuery(id+"F0.wireOp",EDGE,"E9"),sQuery(id+"F0.wireOp",EDGE,"E10"),sQuery(id+"F0.wireOp",EDGE,"E11"),sQuery(id+"F0.wireOp",EDGE,"E12"),sQuery(id+"F0.wireOp",EDGE,"E13"),sQuery(id+"F0.wireOp",EDGE,"E14"),sQuery(id+"F0.wireOp",EDGE,"E15"),sQuery(id+"F0.wireOp",EDGE,"E19.trimOffspring")])]}),"instanceName":"13"});
            var Q16;
            Q16=makeQuery(id+"F3.opPattern","COPY",BODY,{"derivedFrom":makeQuery(id+"F1.opExtrude","SWEPT_BODY",BODY,{"disambiguationData":[OSD([sQuery(id+"F0.wireOp",EDGE,"E0"),sQuery(id+"F0.wireOp",EDGE,"E1"),sQuery(id+"F0.wireOp",EDGE,"E4"),sQuery(id+"F0.wireOp",EDGE,"E5"),sQuery(id+"F0.wireOp",EDGE,"E6"),sQuery(id+"F0.wireOp",EDGE,"E7"),sQuery(id+"F0.wireOp",EDGE,"E8"),sQuery(id+"F0.wireOp",EDGE,"E9"),sQuery(id+"F0.wireOp",EDGE,"E10"),sQuery(id+"F0.wireOp",EDGE,"E11"),sQuery(id+"F0.wireOp",EDGE,"E12"),sQuery(id+"F0.wireOp",EDGE,"E13"),sQuery(id+"F0.wireOp",EDGE,"E14"),sQuery(id+"F0.wireOp",EDGE,"E15"),sQuery(id+"F0.wireOp",EDGE,"E19.trimOffspring")])]}),"instanceName":"11"});
            var Q17;
            Q17=makeQuery(id+"F9.opExtrude","SWEPT_BODY",BODY,{"disambiguationData":[OSD([sQuery(id+"F8.wireOp",EDGE,"E127.0"),sQuery(id+"F8.wireOp",EDGE,"E131.1.3"),sQuery(id+"F8.wireOp",EDGE,"E131.2.3"),sQuery(id+"F8.wireOp",EDGE,"E131.3.3"),sQuery(id+"F8.wireOp",EDGE,"E131.4.3"),sQuery(id+"F8.wireOp",EDGE,"E131.5.3"),sQuery(id+"F8.wireOp",EDGE,"E131.6.3"),sQuery(id+"F8.wireOp",EDGE,"E131.7.3"),sQuery(id+"F8.wireOp",EDGE,"E131.8.3"),sQuery(id+"F8.wireOp",EDGE,"E131.9.3"),sQuery(id+"F8.wireOp",EDGE,"E131.10.3"),sQuery(id+"F8.wireOp",EDGE,"E131.11.3"),sQuery(id+"F8.wireOp",EDGE,"E131.12.3"),sQuery(id+"F8.wireOp",EDGE,"E131.13.3"),sQuery(id+"F8.wireOp",EDGE,"E131.14.3"),sQuery(id+"F8.wireOp",EDGE,"E131.15.3"),sQuery(id+"F8.wireOp",EDGE,"E131.16.3"),sQuery(id+"F8.wireOp",EDGE,"E131.17.3"),sQuery(id+"F8.wireOp",EDGE,"E131.18.3"),sQuery(id+"F8.wireOp",EDGE,"E131.19.3"),sQuery(id+"F8.wireOp",EDGE,"E132"),sQuery(id+"F8.wireOp",EDGE,"E133"),sQuery(id+"F8.wireOp",EDGE,"E134"),sQuery(id+"F8.wireOp",EDGE,"E135"),sQuery(id+"F8.wireOp",EDGE,"E136.1.0"),sQuery(id+"F8.wireOp",EDGE,"E136.1.1"),sQuery(id+"F8.wireOp",EDGE,"E136.2.0"),sQuery(id+"F8.wireOp",EDGE,"E136.2.1"),sQuery(id+"F8.wireOp",EDGE,"E136.3.0"),sQuery(id+"F8.wireOp",EDGE,"E136.3.1"),sQuery(id+"F8.wireOp",EDGE,"E136.4.0"),sQuery(id+"F8.wireOp",EDGE,"E136.4.1"),sQuery(id+"F8.wireOp",EDGE,"E136.5.0"),sQuery(id+"F8.wireOp",EDGE,"E136.5.1"),sQuery(id+"F8.wireOp",EDGE,"E136.6.0"),sQuery(id+"F8.wireOp",EDGE,"E136.6.1"),sQuery(id+"F8.wireOp",EDGE,"E136.7.0"),sQuery(id+"F8.wireOp",EDGE,"E136.7.1"),sQuery(id+"F8.wireOp",EDGE,"E136.8.0"),sQuery(id+"F8.wireOp",EDGE,"E136.8.1"),sQuery(id+"F8.wireOp",EDGE,"E136.9.0"),sQuery(id+"F8.wireOp",EDGE,"E136.9.1"),sQuery(id+"F8.wireOp",EDGE,"E136.10.0"),sQuery(id+"F8.wireOp",EDGE,"E136.10.1"),sQuery(id+"F8.wireOp",EDGE,"E136.11.0"),sQuery(id+"F8.wireOp",EDGE,"E136.11.1"),sQuery(id+"F8.wireOp",EDGE,"E136.12.0"),sQuery(id+"F8.wireOp",EDGE,"E136.12.1"),sQuery(id+"F8.wireOp",EDGE,"E136.13.0"),sQuery(id+"F8.wireOp",EDGE,"E136.13.1"),sQuery(id+"F8.wireOp",EDGE,"E136.14.0"),sQuery(id+"F8.wireOp",EDGE,"E136.14.1"),sQuery(id+"F8.wireOp",EDGE,"E136.15.0"),sQuery(id+"F8.wireOp",EDGE,"E136.15.1"),sQuery(id+"F8.wireOp",EDGE,"E136.16.0"),sQuery(id+"F8.wireOp",EDGE,"E136.16.1"),sQuery(id+"F8.wireOp",EDGE,"E136.17.0"),sQuery(id+"F8.wireOp",EDGE,"E136.17.1"),sQuery(id+"F8.wireOp",EDGE,"E136.18.0"),sQuery(id+"F8.wireOp",EDGE,"E136.18.1"),sQuery(id+"F8.wireOp",EDGE,"E136.19.0"),sQuery(id+"F8.wireOp",EDGE,"E136.19.1"),sQuery(id+"F8.wireOp",EDGE,"E137.trimOffspring"),sQuery(id+"F8.wireOp",EDGE,"E138.trimOffspring"),sQuery(id+"F8.wireOp",EDGE,"E139.trimOffspring"),sQuery(id+"F8.wireOp",EDGE,"E140.trimOffspring"),sQuery(id+"F8.wireOp",EDGE,"E141.trimOffspring"),sQuery(id+"F8.wireOp",EDGE,"E142.trimOffspring"),sQuery(id+"F8.wireOp",EDGE,"E143.trimOffspring"),sQuery(id+"F8.wireOp",EDGE,"E144.trimOffspring"),sQuery(id+"F8.wireOp",EDGE,"E145.trimOffspring"),sQuery(id+"F8.wireOp",EDGE,"E146.trimOffspring"),sQuery(id+"F8.wireOp",EDGE,"E147.trimOffspring"),sQuery(id+"F8.wireOp",EDGE,"E148.trimOffspring"),sQuery(id+"F8.wireOp",EDGE,"E149.trimOffspring"),sQuery(id+"F8.wireOp",EDGE,"E150.trimOffspring"),sQuery(id+"F8.wireOp",EDGE,"E151.trimOffspring"),sQuery(id+"F8.wireOp",EDGE,"E152.trimOffspring"),sQuery(id+"F8.wireOp",EDGE,"E153.trimOffspring"),sQuery(id+"F8.wireOp",EDGE,"E154.trimOffspring"),sQuery(id+"F8.wireOp",EDGE,"E155.trimOffspring")])]});
            var Q18;
            Q18=makeQuery(id+"F3.opPattern","COPY",BODY,{"derivedFrom":makeQuery(id+"F1.opExtrude","SWEPT_BODY",BODY,{"disambiguationData":[OSD([sQuery(id+"F0.wireOp",EDGE,"E0"),sQuery(id+"F0.wireOp",EDGE,"E1"),sQuery(id+"F0.wireOp",EDGE,"E4"),sQuery(id+"F0.wireOp",EDGE,"E5"),sQuery(id+"F0.wireOp",EDGE,"E6"),sQuery(id+"F0.wireOp",EDGE,"E7"),sQuery(id+"F0.wireOp",EDGE,"E8"),sQuery(id+"F0.wireOp",EDGE,"E9"),sQuery(id+"F0.wireOp",EDGE,"E10"),sQuery(id+"F0.wireOp",EDGE,"E11"),sQuery(id+"F0.wireOp",EDGE,"E12"),sQuery(id+"F0.wireOp",EDGE,"E13"),sQuery(id+"F0.wireOp",EDGE,"E14"),sQuery(id+"F0.wireOp",EDGE,"E15"),sQuery(id+"F0.wireOp",EDGE,"E19.trimOffspring")])]}),"instanceName":"15"});
            var Q19;
            Q19=makeQuery(id+"F3.opPattern","COPY",BODY,{"derivedFrom":makeQuery(id+"F1.opExtrude","SWEPT_BODY",BODY,{"disambiguationData":[OSD([sQuery(id+"F0.wireOp",EDGE,"E0"),sQuery(id+"F0.wireOp",EDGE,"E1"),sQuery(id+"F0.wireOp",EDGE,"E4"),sQuery(id+"F0.wireOp",EDGE,"E5"),sQuery(id+"F0.wireOp",EDGE,"E6"),sQuery(id+"F0.wireOp",EDGE,"E7"),sQuery(id+"F0.wireOp",EDGE,"E8"),sQuery(id+"F0.wireOp",EDGE,"E9"),sQuery(id+"F0.wireOp",EDGE,"E10"),sQuery(id+"F0.wireOp",EDGE,"E11"),sQuery(id+"F0.wireOp",EDGE,"E12"),sQuery(id+"F0.wireOp",EDGE,"E13"),sQuery(id+"F0.wireOp",EDGE,"E14"),sQuery(id+"F0.wireOp",EDGE,"E15"),sQuery(id+"F0.wireOp",EDGE,"E19.trimOffspring")])]}),"instanceName":"18"});
            var Q20;
            Q20=makeQuery(id+"F3.opPattern","COPY",BODY,{"derivedFrom":makeQuery(id+"F1.opExtrude","SWEPT_BODY",BODY,{"disambiguationData":[OSD([sQuery(id+"F0.wireOp",EDGE,"E0"),sQuery(id+"F0.wireOp",EDGE,"E1"),sQuery(id+"F0.wireOp",EDGE,"E4"),sQuery(id+"F0.wireOp",EDGE,"E5"),sQuery(id+"F0.wireOp",EDGE,"E6"),sQuery(id+"F0.wireOp",EDGE,"E7"),sQuery(id+"F0.wireOp",EDGE,"E8"),sQuery(id+"F0.wireOp",EDGE,"E9"),sQuery(id+"F0.wireOp",EDGE,"E10"),sQuery(id+"F0.wireOp",EDGE,"E11"),sQuery(id+"F0.wireOp",EDGE,"E12"),sQuery(id+"F0.wireOp",EDGE,"E13"),sQuery(id+"F0.wireOp",EDGE,"E14"),sQuery(id+"F0.wireOp",EDGE,"E15"),sQuery(id+"F0.wireOp",EDGE,"E19.trimOffspring")])]}),"instanceName":"10"});
            var Q21;
            Q21=makeQuery(id+"F3.opPattern","COPY",BODY,{"derivedFrom":makeQuery(id+"F1.opExtrude","SWEPT_BODY",BODY,{"disambiguationData":[OSD([sQuery(id+"F0.wireOp",EDGE,"E0"),sQuery(id+"F0.wireOp",EDGE,"E1"),sQuery(id+"F0.wireOp",EDGE,"E4"),sQuery(id+"F0.wireOp",EDGE,"E5"),sQuery(id+"F0.wireOp",EDGE,"E6"),sQuery(id+"F0.wireOp",EDGE,"E7"),sQuery(id+"F0.wireOp",EDGE,"E8"),sQuery(id+"F0.wireOp",EDGE,"E9"),sQuery(id+"F0.wireOp",EDGE,"E10"),sQuery(id+"F0.wireOp",EDGE,"E11"),sQuery(id+"F0.wireOp",EDGE,"E12"),sQuery(id+"F0.wireOp",EDGE,"E13"),sQuery(id+"F0.wireOp",EDGE,"E14"),sQuery(id+"F0.wireOp",EDGE,"E15"),sQuery(id+"F0.wireOp",EDGE,"E19.trimOffspring")])]}),"instanceName":"12"});
            var Q22;
            Q22=makeQuery(id+"F3.opPattern","COPY",BODY,{"derivedFrom":makeQuery(id+"F1.opExtrude","SWEPT_BODY",BODY,{"disambiguationData":[OSD([sQuery(id+"F0.wireOp",EDGE,"E0"),sQuery(id+"F0.wireOp",EDGE,"E1"),sQuery(id+"F0.wireOp",EDGE,"E4"),sQuery(id+"F0.wireOp",EDGE,"E5"),sQuery(id+"F0.wireOp",EDGE,"E6"),sQuery(id+"F0.wireOp",EDGE,"E7"),sQuery(id+"F0.wireOp",EDGE,"E8"),sQuery(id+"F0.wireOp",EDGE,"E9"),sQuery(id+"F0.wireOp",EDGE,"E10"),sQuery(id+"F0.wireOp",EDGE,"E11"),sQuery(id+"F0.wireOp",EDGE,"E12"),sQuery(id+"F0.wireOp",EDGE,"E13"),sQuery(id+"F0.wireOp",EDGE,"E14"),sQuery(id+"F0.wireOp",EDGE,"E15"),sQuery(id+"F0.wireOp",EDGE,"E19.trimOffspring")])]}),"instanceName":"9"});
            var Q23;
            Q23=qCreatedBy(makeId("Top.planeOp"),FACE);
            mirror(context, id + "F10", {"entities" : qUnion([Q0, Q1, Q2, Q3, Q4, Q5, Q6, Q7, Q8, Q9, Q10, Q11, Q12, Q13, Q14, Q15, Q16, Q17, Q18, Q19, Q20, Q21, Q22]), "mirrorPlane" : qUnion([Q23])});
        }
        {
            var Q0;
            Q0=qCreatedBy(makeId("Front.planeOp"),FACE);
            var sketch = newSketch(context, id + "F11", { "sketchPlane" : qUnion([Q0])});
            skLineSegment(sketch, "E156", {"start": v(854.05, 0) * mm, "end": v(-781.3, 0) * mm});
            skSolve(sketch);
        }
        {
            var Q0;
            Q0=sQuery(id+"F11.wireOp",EDGE,"E156");
            var Q1;
            Q1=qCreatedBy(makeId("Front.planeOp"),FACE);
            cPlane(context, id + "F12", {"entities" : qUnion([Q0, Q1]), "cplaneType" : CPlaneType.LINE_ANGLE, "offset" : 25 * mm, "angle" : 45 * degree, "width" : 150 * mm, "height" : 150 * mm});
        }
        {
            var Q0;
            Q0=qCreatedBy(id+"F12.planeOp",FACE);
            cPlane(context, id + "F13", {"entities" : qUnion([Q0]), "cplaneType" : CPlaneType.OFFSET, "offset" : 580 * mm, "width" : 150 * mm, "height" : 150 * mm});
        }
        {
            var Q0;
            Q0=qCreatedBy(id+"F13.planeOp",FACE);
            var sketch = newSketch(context, id + "F14", { "sketchPlane" : qUnion([Q0])});
            skCircle(sketch, "E157", {"center": v(0, 0) * mm, "radius": 400 * mm});
            skSolve(sketch);
        }
        {
            var Q0;
            Q0 = qSketchRegion(id + "F14", true);
            extrude(context, id + "F15", {"entities" : qUnion([Q0]), "operationType" : NewBodyOperationType.REMOVE, "depth" : 25 * mm});
        }
        {
            var Q0;
            Q0=makeQuery(id+"F14.imprint","IMPRINT",FACE,{"disambiguationData":[TD([[makeQuery(id+"F14.imprint","IMPRINT",EDGE,{"derivedFrom":sQuery(id+"F14.wireOp",EDGE,"E157")}),1.0]])]});
            extrude(context, id + "F16", {"entities" : qUnion([Q0]), "depth" : 4 * mm});
        }
        {
            var Q0;
            Q0=makeQuery(id+"F3.opPattern","COPY",FACE,{"derivedFrom":makeQuery(id+"F1.opExtrude","CAP_FACE",FACE,{"disambiguationData":[OSD([sQuery(id+"F0.wireOp",EDGE,"E0"),sQuery(id+"F0.wireOp",EDGE,"E1"),sQuery(id+"F0.wireOp",EDGE,"E4"),sQuery(id+"F0.wireOp",EDGE,"E5"),sQuery(id+"F0.wireOp",EDGE,"E6"),sQuery(id+"F0.wireOp",EDGE,"E7"),sQuery(id+"F0.wireOp",EDGE,"E8"),sQuery(id+"F0.wireOp",EDGE,"E9"),sQuery(id+"F0.wireOp",EDGE,"E10"),sQuery(id+"F0.wireOp",EDGE,"E11"),sQuery(id+"F0.wireOp",EDGE,"E12"),sQuery(id+"F0.wireOp",EDGE,"E13"),sQuery(id+"F0.wireOp",EDGE,"E14"),sQuery(id+"F0.wireOp",EDGE,"E15"),sQuery(id+"F0.wireOp",EDGE,"E19.trimOffspring")])],"isStart":true}),"instanceName":"16"});
            var sketch = newSketch(context, id + "F17", { "sketchPlane" : qUnion([Q0])});
            skLineSegment(sketch, "E158.0", {"start": v(471.06, -371.62) * mm, "end": v(347.53, -489.1) * mm});
            skLineSegment(sketch, "E159", {"start": v(347.53, -489.1) * mm, "end": v(369.13, -511.8) * mm});
            skLineSegment(sketch, "E160", {"start": v(369.13, -511.8) * mm, "end": v(491.63, -395.3) * mm});
            skLineSegment(sketch, "E161", {"start": v(491.63, -395.3) * mm, "end": v(471.06, -371.62) * mm});
            skSolve(sketch);
        }
        {
            var Q0;
            Q0 = qSketchRegion(id + "F17", true);
            extrude(context, id + "F18", {"entities" : qUnion([Q0]), "operationType" : NewBodyOperationType.REMOVE, "oppositeDirection" : true, "depth" : 25 * mm});
        }
        {
            var Q0;
            Q0=makeQuery(id+"F3.opPattern","COPY",FACE,{"derivedFrom":makeQuery(id+"F1.opExtrude","CAP_FACE",FACE,{"disambiguationData":[OSD([sQuery(id+"F0.wireOp",EDGE,"E0"),sQuery(id+"F0.wireOp",EDGE,"E1"),sQuery(id+"F0.wireOp",EDGE,"E4"),sQuery(id+"F0.wireOp",EDGE,"E5"),sQuery(id+"F0.wireOp",EDGE,"E6"),sQuery(id+"F0.wireOp",EDGE,"E7"),sQuery(id+"F0.wireOp",EDGE,"E8"),sQuery(id+"F0.wireOp",EDGE,"E9"),sQuery(id+"F0.wireOp",EDGE,"E10"),sQuery(id+"F0.wireOp",EDGE,"E11"),sQuery(id+"F0.wireOp",EDGE,"E12"),sQuery(id+"F0.wireOp",EDGE,"E13"),sQuery(id+"F0.wireOp",EDGE,"E14"),sQuery(id+"F0.wireOp",EDGE,"E15"),sQuery(id+"F0.wireOp",EDGE,"E19.trimOffspring")])],"isStart":false}),"instanceName":"14"});
            var sketch = newSketch(context, id + "F19", { "sketchPlane" : qUnion([Q0])});
            skLineSegment(sketch, "E162.0", {"start": v(-471.06, -371.62) * mm, "end": v(-347.53, -489.1) * mm});
            skLineSegment(sketch, "E163", {"start": v(-471.06, -371.62) * mm, "end": v(-520.64, -393.12) * mm});
            skLineSegment(sketch, "E164", {"start": v(-520.64, -393.12) * mm, "end": v(-370.88, -535.54) * mm});
            skLineSegment(sketch, "E165", {"start": v(-370.88, -535.54) * mm, "end": v(-347.53, -489.1) * mm});
            skSolve(sketch);
        }
        {
            var Q0;
            Q0 = qSketchRegion(id + "F19", true);
            extrude(context, id + "F20", {"entities" : qUnion([Q0]), "operationType" : NewBodyOperationType.REMOVE, "oppositeDirection" : true, "depth" : 25 * mm});
        }
        {
            var Q0;
            {var subQ0=sQuery(id+"F0.wireOp",EDGE,"E0");Q0=makeQuery(id+"F15.boolean.opBoolean","COPY",FACE,{"disambiguationData":[TD([makeQuery(id+"F3.opPattern","COPY",FACE,{"derivedFrom":makeQuery(id+"F1.opExtrude","SWEPT_FACE",FACE,{"disambiguationData":[OSD([subQ0])]}),"instanceName":"15"})])],"derivedFrom":makeQuery(id+"F15.opExtrude","CAP_FACE",FACE,{"disambiguationData":[OSD([sQuery(id+"F14.wireOp",EDGE,"E157")])],"isStart":true})});}
            var sketch = newSketch(context, id + "F21", { "sketchPlane" : qUnion([Q0])});
            skLineSegment(sketch, "E166.0", {"start": v(-2, 153.62) * mm, "end": v(-2, -153.62) * mm});
            skLineSegment(sketch, "E167.0", {"start": v(2, 153.62) * mm, "end": v(2, -153.62) * mm});
            skLineSegment(sketch, "E168.bottom", {"start": v(-2, -75) * mm, "end": v(2, -75) * mm});
            skLineSegment(sketch, "E168.top", {"start": v(-2, 75) * mm, "end": v(2, 75) * mm});
            skLineSegment(sketch, "E168.left", {"start": v(-2, -75) * mm, "end": v(-2, 75) * mm});
            skLineSegment(sketch, "E168.right", {"start": v(2, -75) * mm, "end": v(2, 75) * mm});
            skPoint(sketch, "E168.middle", {"position": v(0, 0) * mm});
            skSolve(sketch);
        }
        {
            var Q0;
            Q0 = qSketchRegion(id + "F21", true);
            extrude(context, id + "F22", {"entities" : qUnion([Q0]), "operationType" : NewBodyOperationType.ADD, "depth" : 2 * mm});
        }
        {
            var Q0;
            Q0=makeQuery(id+"F16.opExtrude","CAP_FACE",FACE,{"disambiguationData":[OSD([sQuery(id+"F14.wireOp",EDGE,"E157")])],"isStart":false});
            var sketch = newSketch(context, id + "F23", { "sketchPlane" : qUnion([Q0])});
            skLineSegment(sketch, "E169.0", {"start": v(-2, 75) * mm, "end": v(-2, -75) * mm});
            skLineSegment(sketch, "E170.0", {"start": v(2, 75) * mm, "end": v(2, -75) * mm});
            skLineSegment(sketch, "E171.0", {"start": v(-2, -75) * mm, "end": v(2, -75) * mm});
            skLineSegment(sketch, "E172.0", {"start": v(-2, 75) * mm, "end": v(2, 75) * mm});
            skSolve(sketch);
        }
        {
            var Q0;
            Q0 = qSketchRegion(id + "F23", true);
            extrude(context, id + "F24", {"entities" : qUnion([Q0]), "operationType" : NewBodyOperationType.REMOVE, "oppositeDirection" : true, "depth" : 25 * mm});
        }
        {
            var Q0;
            Q0=qCreatedBy(makeId("Right.planeOp"),FACE);
            var sketch = newSketch(context, id + "F25", { "sketchPlane" : qUnion([Q0])});
            skLineSegment(sketch, "E173", {"start": v(-359.56, 0) * mm, "end": v(354.66, 0) * mm});
            skArc(sketch, "E174", {"start": v(-200, 0) * mm, "mid": v(0, -200) * mm, "end": v(200, 0) * mm});
            skSolve(sketch);
        }
        {
            var Q0;
            Q0 = qSketchRegion(id + "F25", true);
            var Q1;
            Q1=sQuery(id+"F25.wireOp",EDGE,"E173");
            revolve(context, id + "F26", {"entities" : qUnion([Q0]), "axis" : qUnion([Q1]), "revolveType" : RevolveType.FULL});
        }
        {
            var Q0;
            Q0=qCreatedBy(makeId("Top.planeOp"),FACE);
            var sketch = newSketch(context, id + "F27", { "sketchPlane" : qUnion([Q0])});
            skCircle(sketch, "E175", {"center": v(0, 0) * mm, "radius": 30 * mm});
            skCircle(sketch, "E176", {"center": v(0, 0) * mm, "radius": 28 * mm});
            skSolve(sketch);
        }
        {
            var Q0;
            Q0 = qSketchRegion(id + "F27", true);
            extrude(context, id + "F28", {"entities" : qUnion([Q0]), "oppositeDirection" : true, "depth" : 600 * mm});
        }
    });
